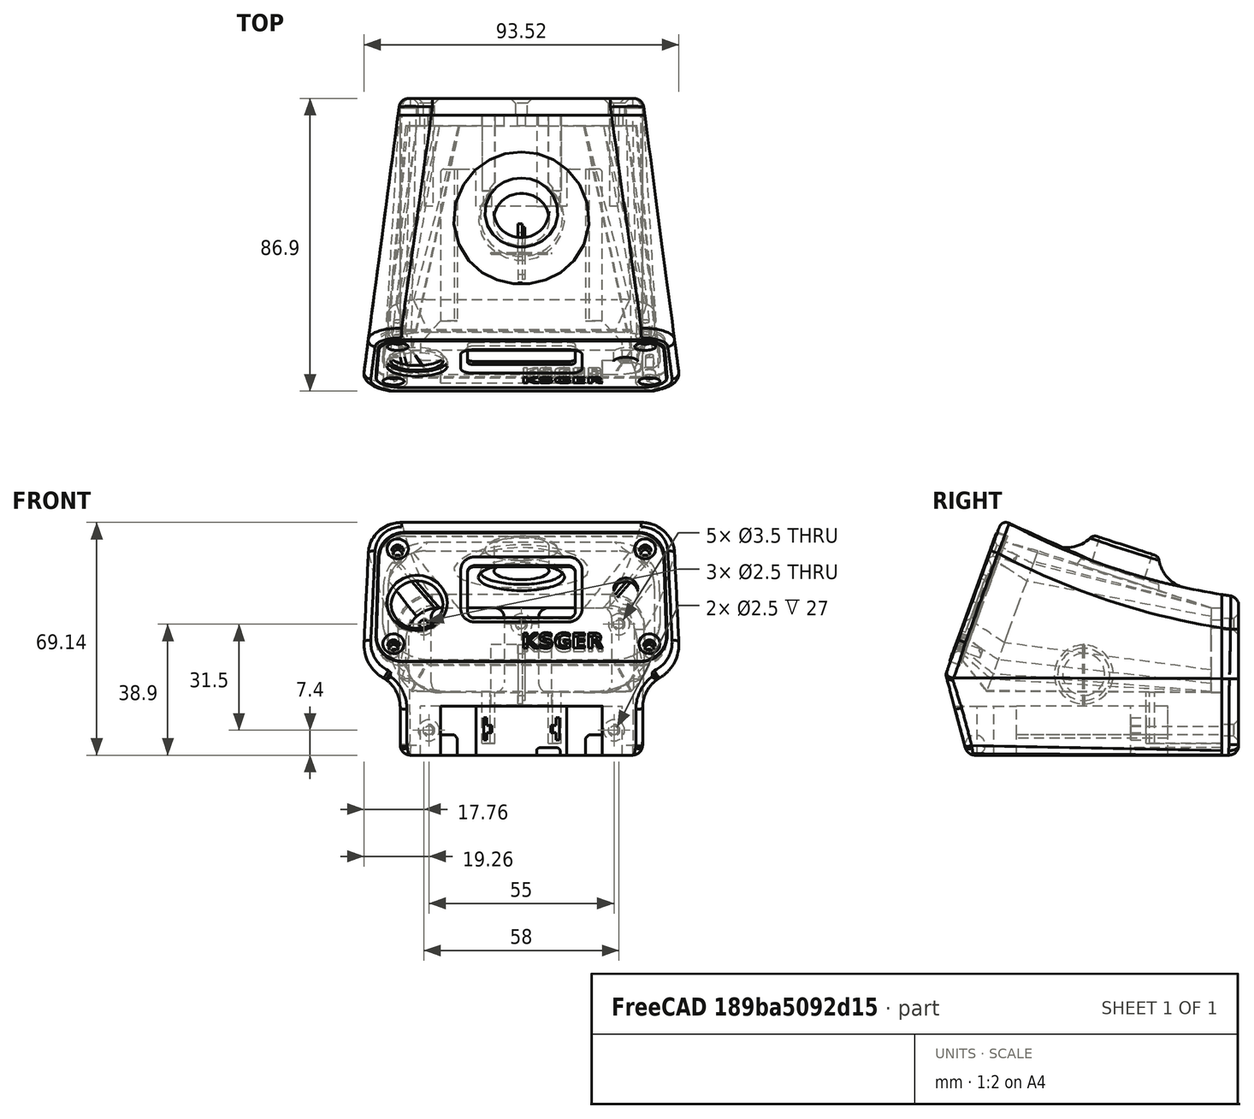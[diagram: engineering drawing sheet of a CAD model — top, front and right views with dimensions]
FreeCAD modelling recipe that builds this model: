
FCSTD DOCUMENT  (FreeCAD 2022.709R28846 (Git))
Label: solder_station5a_snap
License: All rights reserved
LicenseURL: http://en.wikipedia.org/wiki/All_rights_reserved
objects: Sketcher::SketchObject×22, PartDesign::Pocket×12, Part::FeaturePython×6, PartDesign::Fillet×6, Mesh::Feature×5, App::DocumentObjectGroup×4, PartDesign::Body×4, PartDesign::Chamfer×3, PartDesign::FeatureBase×2, PartDesign::Pad×2, PartDesign::Revolution×2, Spreadsheet::Sheet×1, Part::Plane×1, Part::Loft×1, Part::Extrusion×1, Part::MultiCommon×1, Part::Box×1, PartDesign::SubtractiveLoft×1, PartDesign::Groove×1, Part::Part2DObjectPython×1, +2 more types
note: 124 computed .brp shape members not serialized (recipe doc carries the construction recipe); baked Part::Feature solids carry a one-line shape summary decoded from their .brp

FEATURE [Sketcher::SketchObject] Sketch  label="RearSupport"
  ArcFitTolerance = 0
  AttachmentOffset = pos=(0,0,-37.8) rot=(0,0,1;0rad)
  AttachmentSupport = -> [XZ_Plane005]
  FullyConstrained = true
  MapMode = 5
  Placement = pos=(0,37.8,8.4e-15) rot=(1,0,0;1.5708rad)
  Support = -> [XZ_Plane005]
  TreeRank = 0
  expr: AttachmentOffset.Base.z = -<<param>>.mid_depth / 2 + <<param>>.wall
  expr: Constraints[24] = 3
  expr: Constraints[37] = <<param>>.bottom_height
  expr: Constraints[38] = <<param>>.floor
  expr: Constraints[39] = <<param>>.rear_height - <<param>>.wall
  expr: Constraints[47] = <<param>>.reart_screw_width2
  expr: Constraints[48] = <<param>>.rear_screw_width1
  expr: Constraints[49] = <<param>>.screw_hole
  expr: Constraints[50] = <<param>>.rear_screw_height
  expr: Constraints[51] = <<param>>.rear_screw_height
  expr: Constraints[52] = <<param>>.rear_screw_offset
  sketch-geometry (22):
    g0: LineSegment StartX=-23.8 StartY=19.8 StartZ=0 EndX=-8.1 EndY=19.8 EndZ=0
    g1: LineSegment StartX=26.8 StartY=16.8 StartZ=0 EndX=26.8 EndY=-2.4 EndZ=0
    g2: LineSegment StartX=23.8 StartY=-5.4 StartZ=0 EndX=8.1 EndY=-5.4 EndZ=0
    g3: LineSegment StartX=-26.8 StartY=-2.4 StartZ=0 EndX=-26.8 EndY=16.8 EndZ=0
    g4: LineSegment StartX=-5.1 StartY=16.8 StartZ=0 EndX=-5.1 EndY=-2.4 EndZ=0
    g5: LineSegment StartX=5.1 StartY=16.8 StartZ=0 EndX=5.1 EndY=-2.4 EndZ=0
    g6: LineSegment StartX=8.1 StartY=19.8 StartZ=0 EndX=23.8 EndY=19.8 EndZ=0
    g7: LineSegment StartX=-8.1 StartY=-5.4 StartZ=0 EndX=-23.8 EndY=-5.4 EndZ=0
    g8: ArcOfCircle CenterX=-8.1 CenterY=16.8 CenterZ=0 NormalX=0 NormalY=0 NormalZ=1 AngleXU=0 Radius=3 StartAngle=0 EndAngle=1.5708
    g9: ArcOfCircle CenterX=8.1 CenterY=16.8 CenterZ=0 NormalX=0 NormalY=0 NormalZ=1 AngleXU=0 Radius=3 StartAngle=1.5708 EndAngle=3.14159
    g10: ArcOfCircle CenterX=-8.1 CenterY=-2.4 CenterZ=0 NormalX=0 NormalY=0 NormalZ=1 AngleXU=0 Radius=3 StartAngle=4.71239 EndAngle=6.28319
    g11: ArcOfCircle CenterX=8.1 CenterY=-2.4 CenterZ=0 NormalX=0 NormalY=0 NormalZ=1 AngleXU=0 Radius=3 StartAngle=3.14159 EndAngle=4.71239
    g12: ArcOfCircle CenterX=-23.8 CenterY=16.8 CenterZ=0 NormalX=0 NormalY=0 NormalZ=1 AngleXU=0 Radius=3 StartAngle=1.5708 EndAngle=3.14159
    g13: ArcOfCircle CenterX=-23.8 CenterY=-2.4 CenterZ=0 NormalX=0 NormalY=0 NormalZ=1 AngleXU=0 Radius=3 StartAngle=3.14159 EndAngle=4.71239
    g14: ArcOfCircle CenterX=23.8 CenterY=16.8 CenterZ=0 NormalX=0 NormalY=0 NormalZ=1 AngleXU=0 Radius=3 StartAngle=3e-16 EndAngle=1.5708
    g15: ArcOfCircle CenterX=23.8 CenterY=-2.4 CenterZ=0 NormalX=0 NormalY=0 NormalZ=1 AngleXU=0 Radius=3 StartAngle=4.71239 EndAngle=6.28319
    g16: Circle [constr] CenterX=0 CenterY=-24 CenterZ=0 NormalX=0 NormalY=0 NormalZ=1 AngleXU=0 Radius=3
    g17: Circle CenterX=0 CenterY=14.9 CenterZ=0 NormalX=0 NormalY=0 NormalZ=1 AngleXU=0 Radius=1.25
    g18: Circle CenterX=-29 CenterY=14.9 CenterZ=0 NormalX=0 NormalY=0 NormalZ=1 AngleXU=0 Radius=1.25
    g19: Circle [constr] CenterX=-27.5 CenterY=-16.6 CenterZ=0 NormalX=0 NormalY=0 NormalZ=1 AngleXU=0 Radius=1.25
    g20: Circle [constr] CenterX=27.5 CenterY=-16.6 CenterZ=0 NormalX=0 NormalY=0 NormalZ=1 AngleXU=0 Radius=1.25
    g21: Circle CenterX=29 CenterY=14.9 CenterZ=0 NormalX=0 NormalY=0 NormalZ=1 AngleXU=0 Radius=1.25
  constraints (53):
    c: Horizontal(g0)
    c: Horizontal(g2)
    c: Vertical(g1)
    c: Vertical(g3)
    c: Vertical(g4)
    c: Vertical(g5)
    c: Tangent(g0,g6)
    c: Tangent(g2,g7)
    c: Tangent(g0,g8) = 1.5708
    c: Tangent(g4,g8) = 1.5708
    c: Tangent(g5,g9) = -1.5708
    c: Tangent(g6,g9) = 1.5708
    c: Tangent(g7,g10) = 1.5708
    c: Tangent(g4,g10) = 1.5708
    c: Tangent(g5,g11) = -1.5708
    c: Tangent(g2,g11) = 1.5708
    c: Tangent(g0,g12) = 1.5708
    c: Tangent(g3,g12) = 1.5708
    c: Tangent(g3,g13) = 1.5708
    c: Tangent(g7,g13) = 1.5708
    c: Tangent(g6,g14) = 1.5708
    c: Tangent(g1,g14) = 1.5708
    c: Tangent(g1,g15) = 1.5708
    c: Tangent(g2,g15) = 1.5708
    c: Radius(g9) = 3
    c: Equal(g12,g13)
    c: Equal(g13,g10)
    c: Equal(g10,g8)
    c: Equal(g11,g15)
    c: Equal(g15,g14)
    c: Equal(g14,g9)
    c: DistanceX(g4,g-1) = 5.1
    c: DistanceX(g5,g1) = 21.7
    c: Symmetric(g4,g5,g-2)
    c: Equal(g7,g2)
    c: PointOnObject(g16,g-2)
    c: Radius(g16) = 3
    c: DistanceY(g16,g-1) = 24
    c: DistanceY(g16,g2) = 18.6
    c: DistanceY(g16,g6) = 43.8
    c: PointOnObject(g17,g-2)
    c: Equal(g21,g18)
    c: Equal(g18,g19)
    c: Equal(g19,g20)
    c: Equal(g18,g17)
    c: Symmetric(g20,g19,g-2)
    c: Symmetric(g18,g21,g-2)
    c: DistanceX(g19,g20) = 55
    c: DistanceX(g18,g21) = 58
    c: Diameter(g19) = 2.5
    c: DistanceY(g20,g21) = 31.5
    c: DistanceY(g20,g17) = 31.5
    c: DistanceY(g16,g19) = 7.4
FEATURE [Spreadsheet::Sheet] Spreadsheet  label="param"
  PythonMode = false
  ShowCells = 0
  TreeRank = 0
  cells = A1=Body; B2=top_depth; C2(top_depth)=70; B3=mid_depth; C3(mid_depth)=82; D3=half is rear reference; B4=bottom_depth; C4(bottom_depth)=75; B6=bottom_width; C6(bottom_width)=72; B7=bottom_height; C7(bottom_height)=24; B8=bottom_angle; C8(bottom_angle)=15; B10=rear_width; C10(rear_width)=72; B11=rear_height; C11(rear_height)=47; F11=41; B13=mid_width; C13(mid_width)=80; B14=mid_height; C14(mid_height)=56; F14=50; B16=front_width1; C16(front_width1)=92; D16=@top; E16=upper; F16=91; B17=front_width2; C17(front_width2)=95; D17=@mid; E17=lower; F17=94; B18=front_height; C18(front_height)=70; F18=64; B19=front_angle; C19(front_angle)=20; B21=wall; C21(wall)=3.2; B22=radius_big; C22(radius_big)=10; B23=radius_small; C23(radius_small)=3; B24=arch; C24(arch)=200; A26=Button; B27=button_offset; C27(button_offset)=10; B28=button_inside_dia; C28(button_inside_dia)=20; B29=button_outside_dia; C29(button_outside_dia)=22; B30=button_height; C30(button_height)=30.6; F30=26; B31=button_extension; C31(button_extension)=8; B32=button_fillet; C32(button_fillet)=12; B33=button_angle; C33(button_angle)=-18; F33=-17; B34=button_hole; C34(button_hole)=16.4; B35=button_hole_center; C35(button_hole_center)=-0.5; A37=Battery Cuts; B38=batt_carveout; C38(batt_carveout)=14.6; B39=batt_rail; C39(batt_rail)=6; B40=batt_rail_length; C40(batt_rail_length)=45; A42=Terminals; B43=terminal_height; C43(terminal_height)=6.6; B44=terminal_thickness; C44(terminal_thickness)=1; B45=terminal_seperation; C45(terminal_seperation)=21.5; B46=terminal_offset; C46(terminal_offset)=4.5; B47=terminal_depth; C47(terminal_depth)=22.5; A49=Box Interior; B50=floor; C50(floor)=18.6; B51=rear_inside_width; C51(rear_inside_width)==C10 - C21; D51=calc; B52=rear_inside_height; C52(rear_inside_height)==C11 - C21; D52=calc; B53=mid_inside_width; C53(mid_inside_width)==C13; D53=calc; B54=mid_inside_height; C54(mid_inside_height)==C14 + 7; D54=calc; F54=6; B55=front_inside_width1; C55(front_inside_width1)==C62 - C58 * 2; D55=calc; E55=upper; B56=front_inside_width2; C56(front_inside_width2)==C63 - C58 * 2; D56=calc; E56=lower; B57=front_inside_height; C57(front_inside_height)==C64 - C59 * 2; D57=calc; B58=front_width_lip_width; C58(front_width_lip_width)=3; B59=front_inside_lip_height; C59(front_inside_lip_height)=2; A61=Face; B62=face_width1; C62(face_width1)==84 + 1; B63=face_width2; C63(face_width2)==85.5 + 1; B64=face_height; C64(face_height)=41; F64=35; B65=face_thickness; C65(face_thickness)=3; B66=face_radius; C66(face_radius)=8; B67=face_offset; C67(face_offset)=2.8; F67=2.8; A69=Screws; B70=screw_hole; C70(screw_hole)=2.5; B72=front_screw_width1; C72(front_screw_width1)=73.5; D72=upper; B73=front_screw_width2; C73(front_screw_width2)=76; D73=lower; B74=front_screw_height; C74(front_screw_height)=30; F74=24; B75=front_screw_offset; C75(front_screw_offset)=5.5; B77=rear_screw_width1; C77(rear_screw_width1)=58; B78=reart_screw_width2; C78(reart_screw_width2)=55; B79=rear_screw_height; C79(rear_screw_height)=31.5; F79=25.5; B80=rear_screw_offset; C80(rear_screw_offset)=7.4; A82=Back; B83=back_thickness; C83(back_thickness)=5
FEATURE [Sketcher::SketchObject] Sketch008  label="SketchButtonHole"
  ArcFitTolerance = 0
  AttachmentOffset = pos=(0,-0.5,30.6) rot=(1,0,0;-0.314159rad)
  AttachmentSupport = -> [XY_Plane005]
  FullyConstrained = true
  MapMode = 5
  Placement = pos=(0,-0.5,30.6) rot=(1,0,0;5.96903rad)
  Support = -> [XY_Plane005]
  TreeRank = 0
  expr: AttachmentOffset.Base.y = <<param>>.button_hole_center
  expr: AttachmentOffset.Base.z = <<param>>.button_height
  expr: AttachmentOffset.Rotation.Angle = <<param>>.button_angle
  expr: Constraints[0] = <<param>>.button_hole
  expr: Constraints[2] = <<param>>.button_offset
  sketch-geometry (1):
    g0: Circle CenterX=0 CenterY=10 CenterZ=0 NormalX=0 NormalY=0 NormalZ=1 AngleXU=0 Radius=8.2
  constraints (3):
    c: Diameter(g0) = 16.4
    c: PointOnObject(g0,g-2)
    c: DistanceY(g-1,g0) = 10
FEATURE [Sketcher::SketchObject] Sketch012  label="SketchSide"
  ArcFitTolerance = 0
  AttachmentOffset = pos=(2.5,0,0) rot=(0,0,1;0rad)
  AttachmentSupport = -> [YZ_Plane006]
  FullyConstrained = true
  MapMode = 5
  Placement = pos=(6e-16,2.5,-6e-16) rot=(0.57735,0.57735,0.57735;2.0944rad)
  Support = -> [YZ_Plane006]
  TreeRank = 0
  expr: AttachmentOffset.Base.x = <<param>>.back_thickness / 2
  expr: Constraints[14] = <<param>>.bottom_height
  expr: Constraints[15] = <<param>>.radius_small
  expr: Constraints[16] = 90 - <<param>>.bottom_angle
  expr: Constraints[17] = 90 - <<param>>.front_angle
  expr: Constraints[21] = <<param>>.front_height
  expr: Constraints[4] = <<param>>.rear_height - <<param>>.bottom_height
  expr: Constraints[5] = <<param>>.arch
  expr: Constraints[6] = <<param>>.mid_depth + <<param>>.back_thickness
  sketch-geometry (7):
    g0: LineSegment StartX=43.5 StartY=0 StartZ=0 EndX=43.5 EndY=23 EndZ=0
    g1: LineSegment StartX=-43.5 StartY=0 StartZ=0 EndX=-26.7574 EndY=46 EndZ=0
    g2: ArcOfCircle CenterX=69.5235 CenterY=221.3 CenterZ=0 NormalX=0 NormalY=0 NormalZ=1 AngleXU=0 Radius=200 StartAngle=4.21013 EndAngle=4.5819
    g3: LineSegment StartX=-43.5 StartY=0 StartZ=0 EndX=-37.665 EndY=-21.7765 EndZ=0
    g4: LineSegment StartX=-34.7673 StartY=-24 StartZ=0 EndX=43.5 EndY=-24 EndZ=0
    g5: LineSegment StartX=43.5 StartY=-24 StartZ=0 EndX=43.5 EndY=0 EndZ=0
    g6: ArcOfCircle CenterX=-34.7672 CenterY=-21 CenterZ=0 NormalX=0 NormalY=0 NormalZ=1 AngleXU=0 Radius=3 StartAngle=3.4034 EndAngle=4.71238
  constraints (22):
    c: PointOnObject(g1,g-1)
    c: Vertical(g0)
    c: Coincident(g2,g0)
    c: Symmetric(g1,g0,g-2)
    c: DistanceY(g0,g0) = 23
    c: Radius(g2) = 200
    c: DistanceX(g1,g0) = 87
    c: Horizontal(g4)
    c: Coincident(g5,g4)
    c: Vertical(g5)
    c: Coincident(g6,g3)
    c: Coincident(g6,g4)
    c: Tangent(g6,g4)
    c: Tangent(g6,g3)
    c: DistanceY(g4,g-1) = 24
    c: Radius(g6) = 3
    c: Angle(g3,g-1) = 1.309
    c: Angle(g-1,g1) = 1.22173
    c: Coincident(g3,g1)
    c: Coincident(g5,g0)
    c: Coincident(g2,g1)
    c: DistanceY(g4,g1) = 70
FEATURE [Sketcher::SketchObject] Sketch018  label="SketchBat1"
  ArcFitTolerance = 0
  AttachmentOffset = pos=(0,0,-24) rot=(0,0,1;0rad)
  AttachmentSupport = -> [XY_Plane005]
  FullyConstrained = true
  MapMode = 5
  Placement = pos=(0,0,-24) rot=(0,0,1;0rad)
  Support = -> [XY_Plane005]
  TreeRank = 0
  expr: AttachmentOffset.Base.z = -<<param>>.bottom_height
  expr: Constraints[63] = <<param>>.batt_rail_length
  expr: Constraints[64] = <<param>>.mid_depth / 2
  sketch-geometry (21):
    g0: LineSegment StartX=-24 StartY=-41.7082 StartZ=0 EndX=24 EndY=-41.7082 EndZ=0
    g1: LineSegment StartX=24 StartY=-41.7082 StartZ=0 EndX=24 EndY=-31.7082 EndZ=0
    g2: LineSegment StartX=24 StartY=-31.7082 StartZ=0 EndX=30 EndY=-31.7082 EndZ=0
    g3: LineSegment StartX=30 StartY=-31.7082 StartZ=0 EndX=30 EndY=-26.7082 EndZ=0
    g4: LineSegment StartX=30 StartY=-26.7082 StartZ=0 EndX=24 EndY=-20 EndZ=0
    g5: LineSegment StartX=24 StartY=-20 StartZ=0 EndX=24 EndY=24 EndZ=0
    g6: LineSegment StartX=13.5 StartY=24 StartZ=0 EndX=13.5 EndY=14 EndZ=0
    g7: LineSegment StartX=13.5 StartY=14 StartZ=0 EndX=-13.5 EndY=14 EndZ=0
    g8: LineSegment StartX=-13.5 StartY=14 StartZ=0 EndX=-13.5 EndY=24 EndZ=0
    g9: LineSegment StartX=-24 StartY=24 StartZ=0 EndX=-24 EndY=-20 EndZ=0
    g10: LineSegment StartX=-24 StartY=-20 StartZ=0 EndX=-30 EndY=-26.7082 EndZ=0
    g11: LineSegment StartX=-30 StartY=-26.7082 StartZ=0 EndX=-30 EndY=-31.7082 EndZ=0
    g12: LineSegment StartX=-30 StartY=-31.7082 StartZ=0 EndX=-24 EndY=-31.7082 EndZ=0
    g13: LineSegment StartX=-24 StartY=-31.7082 StartZ=0 EndX=-24 EndY=-41.7082 EndZ=0
    g14: Circle [constr] CenterX=0 CenterY=41 CenterZ=0 NormalX=0 NormalY=0 NormalZ=1 AngleXU=0 Radius=4
    g15: ArcOfCircle CenterX=-14.5 CenterY=24 CenterZ=0 NormalX=0 NormalY=0 NormalZ=1 AngleXU=0 Radius=1 StartAngle=6.28318 EndAngle=7.85399
    g16: LineSegment StartX=-23 StartY=25 StartZ=0 EndX=-14.5 EndY=25 EndZ=0
    g17: LineSegment StartX=14.5 StartY=25 StartZ=0 EndX=23 EndY=25 EndZ=0
    g18: ArcOfCircle CenterX=-23 CenterY=24 CenterZ=0 NormalX=0 NormalY=0 NormalZ=1 AngleXU=0 Radius=1 StartAngle=1.57079 EndAngle=3.1416
    g19: ArcOfCircle CenterX=14.5 CenterY=24 CenterZ=0 NormalX=0 NormalY=0 NormalZ=1 AngleXU=0 Radius=1 StartAngle=1.5708 EndAngle=3.14159
    g20: ArcOfCircle CenterX=23 CenterY=24 CenterZ=0 NormalX=0 NormalY=0 NormalZ=1 AngleXU=0 Radius=1.00001 StartAngle=2.75124e-06 EndAngle=1.5708
  constraints (65):
    c: Horizontal(g0)
    c: Coincident(g1,g0)
    c: Vertical(g1)
    c: Coincident(g2,g1)
    c: Horizontal(g2)
    c: Coincident(g3,g2)
    c: Coincident(g3,g4)
    c: Vertical(g5)
    c: Coincident(g6,g7)
    c: Coincident(g7,g8)
    c: Vertical(g8)
    c: Vertical(g9)
    c: Coincident(g10,g11)
    c: Vertical(g11)
    c: Coincident(g11,g12)
    c: Horizontal(g12)
    c: Coincident(g12,g13)
    c: Equal(g6,g8)
    c: Equal(g5,g9)
    c: Equal(g4,g10)
    c: Equal(g3,g11)
    c: Equal(g12,g2)
    c: Equal(g1,g13)
    c: Coincident(g13,g0)
    c: Vertical(g13)
    c: DistanceX(g7,g7) = 27
    c: Symmetric(g7,g6,g-2)
    c: Distance(g4) = 9
    c: Vertical(g3)
    c: DistanceY(g3,g3) = 5
    c: DistanceX(g2,g2) = 6
    c: DistanceY(g1,g1) = 10
    c: DistanceX(g0,g0) = 48
    c: PointOnObject(g14,g-2)
    c: Coincident(g9,g10)
    c: Coincident(g5,g4)
    c: Coincident(g15,g8)
    c: Coincident(g16,g15)
    c: Tangent(g15,g8)
    c: Horizontal(g16)
    c: Horizontal(g17)
    c: DistanceX(g9,g5) = 48
    c: Symmetric(g4,g9,g-2)
    c: Equal(g16,g17)
    c: Coincident(g18,g9)
    c: Coincident(g18,g16)
    c: Equal(g18,g15)
    c: Tangent(g18,g16)
    c: Tangent(g18,g9)
    c: DistanceY(g6,g17) = 11
    c: Vertical(g6)
    c: Coincident(g19,g6)
    c: Coincident(g19,g17)
    c: Coincident(g20,g17)
    c: Coincident(g20,g5)
    c: Tangent(g20,g17)
    c: Tangent(g20,g5)
    c: Tangent(g19,g6)
    c: Tangent(g19,g17)
    c: Equal(g15,g19)
    c: Radius(g19) = 1
    c: Radius(g14) = 4
    c: DistanceY(g15,g14) = 16
    c: DistanceY(g9,g16) = 45
    c: DistanceY(g-1,g14) = 41
FEATURE [Sketcher::SketchObject] Sketch019  label="SketchBat2"
  ArcFitTolerance = 0
  AttachmentOffset = pos=(0,0,-25) rot=(0,0,1;0rad)
  AttachmentSupport = -> [XZ_Plane005]
  FullyConstrained = true
  MapMode = 5
  Placement = pos=(0,25,5.6e-15) rot=(1,0,0;1.5708rad)
  Support = -> [XZ_Plane005]
  TreeRank = 0
  expr: AttachmentOffset.Base.z = -<<param>>.mid_depth / 2 + 16
  expr: Constraints[17] = <<param>>.bottom_height
  expr: Constraints[18] = <<param>>.batt_rail
  expr: Constraints[19] = 48.01mm
  sketch-geometry (10):
    g0: LineSegment StartX=-24.005 StartY=-18 StartZ=0 EndX=-20.005 EndY=-18 EndZ=0
    g1: LineSegment StartX=-19.005 StartY=-24 StartZ=0 EndX=-24.005 EndY=-24 EndZ=0
    g2: LineSegment StartX=-24.005 StartY=-24 StartZ=0 EndX=-24.005 EndY=-18 EndZ=0
    g3: LineSegment StartX=24.005 StartY=-18 StartZ=0 EndX=20.005 EndY=-18 EndZ=0
    g4: LineSegment StartX=19.005 StartY=-24 StartZ=0 EndX=24.005 EndY=-24 EndZ=0
    g5: LineSegment StartX=24.005 StartY=-24 StartZ=0 EndX=24.005 EndY=-18 EndZ=0
    g6: LineSegment StartX=-19.005 StartY=-19 StartZ=0 EndX=-19.005 EndY=-24 EndZ=0
    g7: LineSegment StartX=19.005 StartY=-24 StartZ=0 EndX=19.005 EndY=-19 EndZ=0
    g8: LineSegment StartX=-20.005 StartY=-18 StartZ=0 EndX=-19.005 EndY=-19 EndZ=0
    g9: LineSegment StartX=19.005 StartY=-19 StartZ=0 EndX=20.005 EndY=-18 EndZ=0
  constraints (29):
    c: Coincident(g1,g2)
    c: Coincident(g2,g0)
    c: Horizontal(g0)
    c: Horizontal(g1)
    c: Vertical(g2)
    c: Coincident(g4,g5)
    c: Coincident(g5,g3)
    c: Horizontal(g3)
    c: Horizontal(g4)
    c: Vertical(g5)
    c: Coincident(g6,g1)
    c: Vertical(g6)
    c: Equal(g1,g4)
    c: Coincident(g7,g4)
    c: Vertical(g7)
    c: Equal(g6,g7)
    c: Symmetric(g1,g4,g-2)
    c: DistanceY(g1,g-1) = 24
    c: DistanceY(g4,g3) = 6
    c: DistanceX(g1,g4) = 48.01
    c: DistanceX(g4,g4) = 5
    c: Coincident(g8,g0)
    c: Coincident(g8,g6)
    c: Coincident(g9,g7)
    c: Coincident(g9,g3)
    c: Equal(g0,g3)
    c: Equal(g2,g5)
    c: DistanceX(g0,g0) = 4
    c: DistanceY(g1,g6) = 5
FEATURE [Sketcher::SketchObject] Sketch021  label="SketchButton"
  ArcFitTolerance = 0
  AttachmentOffset = pos=(10,30.6,0) rot=(0,0,1;-0.314159rad)
  AttachmentSupport = -> [YZ_Plane005]
  FullyConstrained = true
  MapMode = 5
  Placement = pos=(-4.6e-15,10,30.6) rot=(-0.506732,-0.697457,-0.506732;4.35963rad)
  Support = -> [YZ_Plane005]
  TreeRank = 0
  expr: AttachmentOffset.Base.x = <<param>>.button_offset
  expr: AttachmentOffset.Base.y = <<param>>.button_height
  expr: AttachmentOffset.Rotation.Angle = <<param>>.button_angle
  expr: Constraints[6] = <<param>>.button_extension
  expr: Constraints[7] = <<param>>.button_outside_dia / 2
  sketch-geometry (5):
    g0: LineSegment StartX=0 StartY=0 StartZ=0 EndX=0 EndY=8 EndZ=0
    g1: LineSegment StartX=0 StartY=8 StartZ=0 EndX=9 EndY=8 EndZ=0
    g2: LineSegment StartX=0 StartY=0 StartZ=0 EndX=11 EndY=0 EndZ=0
    g3: LineSegment StartX=11 StartY=0 StartZ=0 EndX=11 EndY=6 EndZ=0
    g4: ArcOfCircle CenterX=9 CenterY=6 CenterZ=0 NormalX=0 NormalY=0 NormalZ=1 AngleXU=0 Radius=2 StartAngle=1e-16 EndAngle=1.5708
  constraints (13):
    c: Coincident(g0,g-1)
    c: PointOnObject(g0,g-2)
    c: Coincident(g1,g0)
    c: Horizontal(g1)
    c: Coincident(g2,g0)
    c: Horizontal(g2)
    c: DistanceY(g0,g0) = 8
    c: DistanceX(g2,g2) = 11
    c: Coincident(g3,g2)
    c: Vertical(g3)
    c: Radius(g4) = 2
    c: Tangent(g4,g1) = 1.5708
    c: Tangent(g4,g3) = -1.5708
FEATURE [Sketcher::SketchObject] Sketch022  label="SketchRearInside"
  ArcFitTolerance = 0
  AttachmentOffset = pos=(0,0,-37.8) rot=(0,0,1;0rad)
  AttachmentSupport = -> [XZ_Plane005]
  FullyConstrained = true
  MapMode = 5
  Placement = pos=(0,37.8,8.4e-15) rot=(1,0,0;1.5708rad)
  Support = -> [XZ_Plane005]
  TreeRank = 0
  expr: AttachmentOffset.Base.z = -<<param>>.mid_depth / 2 + <<param>>.wall
  expr: Constraints[12] = <<param>>.radius_big
  expr: Constraints[18] = <<param>>.rear_inside_width
  expr: Constraints[26] = <<param>>.bottom_height
  expr: Constraints[27] = <<param>>.rear_inside_height
  expr: Constraints[29] = <<param>>.floor
  sketch-geometry (9):
    g0: LineSegment StartX=-34.4 StartY=9.80003 StartZ=0 EndX=-34.4 EndY=4.59997 EndZ=0
    g1: LineSegment StartX=-24.4 StartY=-5.4 StartZ=0 EndX=24.4 EndY=-5.4 EndZ=0
    g2: LineSegment StartX=34.4 StartY=4.59997 StartZ=0 EndX=34.4 EndY=9.80003 EndZ=0
    g3: LineSegment StartX=-24.4 StartY=19.8 StartZ=0 EndX=24.4 EndY=19.8 EndZ=0
    g4: ArcOfCircle CenterX=24.4 CenterY=9.8 CenterZ=0 NormalX=0 NormalY=0 NormalZ=1 AngleXU=0 Radius=10 StartAngle=3.49027e-06 EndAngle=1.57079
    g5: ArcOfCircle CenterX=24.4 CenterY=4.6 CenterZ=0 NormalX=0 NormalY=0 NormalZ=1 AngleXU=0 Radius=10 StartAngle=4.71239 EndAngle=6.28318
    g6: ArcOfCircle CenterX=-24.4 CenterY=9.8 CenterZ=0 NormalX=0 NormalY=0 NormalZ=1 AngleXU=0 Radius=10 StartAngle=1.5708 EndAngle=3.14159
    g7: ArcOfCircle CenterX=-24.4 CenterY=4.6 CenterZ=0 NormalX=0 NormalY=0 NormalZ=1 AngleXU=0 Radius=10 StartAngle=3.1416 EndAngle=4.71239
    g8: Circle [constr] CenterX=0 CenterY=-24 CenterZ=0 NormalX=0 NormalY=0 NormalZ=1 AngleXU=0 Radius=3
  constraints (30):
    c: Vertical(g0)
    c: Horizontal(g1)
    c: Vertical(g2)
    c: Horizontal(g3)
    c: Equal(g3,g1)
    c: Equal(g0,g2)
    c: Coincident(g4,g3)
    c: Coincident(g4,g2)
    c: Coincident(g5,g2)
    c: Coincident(g5,g1)
    c: Coincident(g6,g0)
    c: Coincident(g6,g3)
    c: Radius(g6) = 10
    c: Equal(g6,g4)
    c: Equal(g4,g5)
    c: Coincident(g7,g1)
    c: Coincident(g7,g0)
    c: Equal(g5,g7)
    c: DistanceX(g0,g2) = 68.8
    c: Symmetric(g0,g2,g-2)
    c: Tangent(g4,g2)
    c: Tangent(g4,g3)
    c: Tangent(g5,g2)
    c: Tangent(g5,g1)
    c: Tangent(g6,g3)
    c: PointOnObject(g8,g-2)
    c: DistanceY(g8,g-1) = 24
    c: DistanceY(g8,g3) = 43.8
    c: Radius(g8) = 3
    c: DistanceY(g8,g1) = 18.6
FEATURE [Sketcher::SketchObject] Sketch024  label="SketchFaceCut"
  ArcFitTolerance = 0
  AttachmentOffset = pos=(0,0,37.6) rot=(1,0,0;-0.349066rad)
  AttachmentSupport = -> [XZ_Plane005]
  FullyConstrained = true
  MapMode = 5
  Placement = pos=(0,-37.6,-8.3e-15) rot=(-1,0,0;5.06145rad)
  Support = -> [XZ_Plane005]
  TreeRank = 0
  expr: AttachmentOffset.Base.z = <<param>>.mid_depth / 2 - <<param>>.face_thickness - 0.4
  expr: AttachmentOffset.Rotation.Angle = -<<param>>.front_angle
  expr: Constraints[13] = <<param>>.face_radius
  expr: Constraints[22] = <<param>>.face_width1
  expr: Constraints[23] = <<param>>.face_width2
  expr: Constraints[24] = <<param>>.face_offset
  expr: Constraints[25] = <<param>>.face_height
  sketch-geometry (8):
    g0: LineSegment StartX=-34.5035 StartY=43.8 StartZ=0 EndX=34.5037 EndY=43.8 EndZ=0
    g1: LineSegment StartX=42.5001 StartY=36.0399 StartZ=0 EndX=43.25 EndY=11.0399 EndZ=0
    g2: LineSegment StartX=35.2536 StartY=2.8 StartZ=0 EndX=-35.2536 EndY=2.8 EndZ=0
    g3: LineSegment StartX=-43.25 StartY=11.0399 StartZ=0 EndX=-42.4999 EndY=36.0399 EndZ=0
    g4: ArcOfCircle CenterX=34.5037 CenterY=35.8 CenterZ=0 NormalX=0 NormalY=0 NormalZ=1 AngleXU=0 Radius=8 StartAngle=0.0299879 EndAngle=1.5708
    g5: ArcOfCircle CenterX=35.2536 CenterY=10.8 CenterZ=0 NormalX=0 NormalY=0 NormalZ=1 AngleXU=0 Radius=8 StartAngle=4.71239 EndAngle=6.31317
    g6: ArcOfCircle CenterX=-34.5035 CenterY=35.8 CenterZ=0 NormalX=0 NormalY=0 NormalZ=1 AngleXU=0 Radius=8 StartAngle=1.5708 EndAngle=3.1116
    g7: ArcOfCircle CenterX=-35.2536 CenterY=10.8 CenterZ=0 NormalX=0 NormalY=0 NormalZ=1 AngleXU=0 Radius=8 StartAngle=3.1116 EndAngle=4.71239
  constraints (27):
    c: Horizontal(g0)
    c: Coincident(g4,g0)
    c: Coincident(g4,g1)
    c: Coincident(g5,g1)
    c: Coincident(g5,g2)
    c: Coincident(g6,g0)
    c: Coincident(g6,g3)
    c: Coincident(g7,g3)
    c: Coincident(g7,g2)
    c: Equal(g1,g3)
    c: Equal(g4,g6)
    c: Equal(g6,g7)
    c: Equal(g7,g5)
    c: Radius(g4) = 8
    c: Tangent(g6,g3)
    c: Tangent(g7,g3)
    c: Tangent(g7,g2)
    c: Tangent(g6,g0)
    c: Tangent(g4,g0)
    c: Tangent(g4,g1)
    c: Tangent(g5,g1)
    c: Tangent(g5,g2)
    c: DistanceX(g3,g1) = 85
    c: DistanceX(g3,g1) = 86.5
    c: DistanceY(g-1,g2) = 2.8
    c: DistanceY(g2,g0) = 41
    c: Symmetric(g2,g2,g-2)
FEATURE [Sketcher::SketchObject] Sketch025  label="SketchMidInside"
  ArcFitTolerance = 0
  AttachmentOffset = pos=(0,0,27) rot=(1,0,0;-0.349066rad)
  AttachmentSupport = -> [XZ_Plane005]
  FullyConstrained = true
  MapMode = 5
  Placement = pos=(0,-27,-6e-15) rot=(-1,0,0;5.06145rad)
  Support = -> [XZ_Plane005]
  TreeRank = 0
  expr: AttachmentOffset.Base.z = <<param>>.mid_depth / 2 - 14
  expr: AttachmentOffset.Rotation.Angle = -<<param>>.front_angle
  expr: Constraints[10] = <<param>>.radius_big + 1
  expr: Constraints[11] = <<param>>.floor
  expr: Constraints[12] = Spreadsheet.mid_inside_width - 1
  expr: Constraints[14] = <<param>>.mid_inside_height
  expr: Constraints[23] = <<param>>.mid_width - 15
  expr: Constraints[4] = <<param>>.bottom_height
  sketch-geometry (9):
    g0: LineSegment StartX=-28.5 StartY=39 StartZ=0 EndX=28.5 EndY=39 EndZ=0
    g1: LineSegment StartX=39.5 StartY=28 StartZ=0 EndX=39.5 EndY=10 EndZ=0
    g2: LineSegment StartX=32.5 StartY=-5.4 StartZ=0 EndX=-32.5 EndY=-5.4 EndZ=0
    g3: LineSegment StartX=-39.5 StartY=10 StartZ=0 EndX=-39.5 EndY=28 EndZ=0
    g4: Circle [constr] CenterX=0 CenterY=-24 CenterZ=0 NormalX=0 NormalY=0 NormalZ=1 AngleXU=0 Radius=3
    g5: ArcOfCircle CenterX=-28.5 CenterY=28 CenterZ=0 NormalX=0 NormalY=0 NormalZ=1 AngleXU=0 Radius=11 StartAngle=1.5708 EndAngle=3.14159
    g6: ArcOfCircle CenterX=28.5 CenterY=28 CenterZ=0 NormalX=0 NormalY=0 NormalZ=1 AngleXU=0 Radius=11 StartAngle=0 EndAngle=1.5708
    g7: ArcOfCircle CenterX=-15.553 CenterY=11.5941 CenterZ=0 NormalX=0 NormalY=0 NormalZ=1 AngleXU=0 Radius=24 StartAngle=3.20806 EndAngle=3.92838
    g8: ArcOfCircle CenterX=15.553 CenterY=11.5941 CenterZ=0 NormalX=0 NormalY=0 NormalZ=1 AngleXU=0 Radius=24 StartAngle=5.4964 EndAngle=6.21672
  constraints (25):
    c: Vertical(g1)
    c: Vertical(g3)
    c: PointOnObject(g4,g-2)
    c: Radius(g4) = 3
    c: DistanceY(g4,g-1) = 24
    c: Tangent(g3,g5) = 1.5708
    c: Tangent(g0,g5) = 1.5708
    c: Tangent(g0,g6) = 1.5708
    c: Tangent(g1,g6) = 1.5708
    c: Equal(g6,g5)
    c: Radius(g6) = 11
    c: DistanceY(g4,g2) = 18.6
    c: DistanceX(g3,g1) = 79
    c: Symmetric(g2,g2,g-2)
    c: DistanceY(g4,g0) = 63
    c: Symmetric(g0,g0,g-2)
    c: Equal(g3,g1)
    c: Coincident(g7,g2)
    c: Coincident(g8,g1)
    c: Coincident(g8,g2)
    c: Coincident(g7,g3)
    c: Equal(g8,g7)
    c: Radius(g8) = 24
    c: DistanceX(g2,g2) = 65
    c: DistanceY(g1,g1) = 18
FEATURE [Sketcher::SketchObject] Sketch026  label="SketchFrontScrews"
  ArcFitTolerance = 0
  AttachmentOffset = pos=(0,0,38) rot=(1,0,0;-0.349066rad)
  AttachmentSupport = -> [XZ_Plane005]
  FullyConstrained = true
  MapMode = 5
  Placement = pos=(0,-38,-8.4e-15) rot=(-1,0,0;5.06145rad)
  Support = -> [XZ_Plane005]
  TreeRank = 0
  expr: AttachmentOffset.Base.z = <<param>>.mid_depth / 2 - <<param>>.face_thickness
  expr: AttachmentOffset.Rotation.Angle = -<<param>>.front_angle
  expr: Constraints[0] = <<param>>.front_screw_width1
  expr: Constraints[13] = <<param>>.screw_hole
  expr: Constraints[1] = <<param>>.front_screw_width2
  expr: Constraints[2] = <<param>>.front_screw_height
  expr: Constraints[9] = <<param>>.face_offset + <<param>>.front_screw_offset
  sketch-geometry (6):
    g0: Circle CenterX=-36.75 CenterY=38.3 CenterZ=0 NormalX=0 NormalY=0 NormalZ=1 AngleXU=0 Radius=1.25
    g1: Circle CenterX=36.75 CenterY=38.3 CenterZ=0 NormalX=0 NormalY=0 NormalZ=1 AngleXU=0 Radius=1.25
    g2: Circle CenterX=-38 CenterY=8.3 CenterZ=0 NormalX=0 NormalY=0 NormalZ=1 AngleXU=0 Radius=1.25
    g3: Circle CenterX=38 CenterY=8.3 CenterZ=0 NormalX=0 NormalY=0 NormalZ=1 AngleXU=0 Radius=1.25
    g4: LineSegment [constr] StartX=-36.75 StartY=38.3 StartZ=0 EndX=36.75 EndY=38.3 EndZ=0
    g5: LineSegment [constr] StartX=-38 StartY=8.3 StartZ=0 EndX=38 EndY=8.3 EndZ=0
  constraints (14):
    c: DistanceX(g0,g1) = 73.5
    c: DistanceX(g2,g3) = 76
    c: DistanceY(g3,g1) = 30
    c: Coincident(g4,g0)
    c: Coincident(g4,g1)
    c: Coincident(g5,g2)
    c: Coincident(g5,g3)
    c: Symmetric(g2,g3,g-2)
    c: Symmetric(g0,g1,g-2)
    c: DistanceY(g-1,g3) = 8.3
    c: Equal(g0,g2)
    c: Equal(g2,g3)
    c: Equal(g3,g1)
    c: Diameter(g0) = 2.5
FEATURE [Sketcher::SketchObject] Sketch023  label="SketchFrontInside"
  ArcFitTolerance = 0
  AttachmentOffset = pos=(0,0,38) rot=(1,0,0;-0.349066rad)
  AttachmentSupport = -> [XZ_Plane005]
  ExternalGeometry = -> [Sketch026,Sketch024]
  FullyConstrained = true
  MapMode = 5
  Placement = pos=(0,-38,-8.4e-15) rot=(-1,0,0;5.06145rad)
  Support = -> [XZ_Plane005]
  TreeRank = 0
  expr: AttachmentOffset.Base.z = <<param>>.mid_depth / 2 - <<param>>.face_thickness
  expr: AttachmentOffset.Rotation.Angle = -<<param>>.front_angle
  sketch-geometry (16):
    g0: LineSegment StartX=-27.5 StartY=4.93681 StartZ=0 EndX=27.5 EndY=4.93681 EndZ=0
    g1: LineSegment StartX=27.5 StartY=41.9368 StartZ=0 EndX=-27.5 EndY=41.9368 EndZ=0
    g2: LineSegment StartX=-40.95 StartY=28.0001 StartZ=0 EndX=-41.25 EndY=18.0001 EndZ=0
    g3: LineSegment StartX=40.95 StartY=28 StartZ=0 EndX=41.25 EndY=18 EndZ=0
    g4: ArcOfCircle CenterX=36.75 CenterY=38.3 CenterZ=0 NormalX=0 NormalY=0 NormalZ=1 AngleXU=0 Radius=3 StartAngle=2.46996 EndAngle=5.23357
    g5: ArcOfCircle CenterX=27.5 CenterY=27.5965 CenterZ=0 NormalX=0 NormalY=0 NormalZ=1 AngleXU=0 Radius=13.4561 StartAngle=0.0299886 EndAngle=0.646116
    g6: ArcOfCircle CenterX=27.5 CenterY=27.5965 CenterZ=0 NormalX=0 NormalY=0 NormalZ=1 AngleXU=0 Radius=14.3403 StartAngle=1.06869 EndAngle=1.5708
    g7: ArcOfCircle CenterX=38 CenterY=8.3 CenterZ=0 NormalX=0 NormalY=0 NormalZ=1 AngleXU=0 Radius=3 StartAngle=1.04133 EndAngle=3.41706
    g8: ArcOfCircle CenterX=27.5 CenterY=17.5875 CenterZ=0 NormalX=0 NormalY=0 NormalZ=1 AngleXU=0 Radius=13.7562 StartAngle=5.77461 EndAngle=6.31317
    g9: ArcOfCircle CenterX=27.5 CenterY=17.5875 CenterZ=0 NormalX=0 NormalY=0 NormalZ=1 AngleXU=0 Radius=12.6507 StartAngle=4.71239 EndAngle=5.35813
    g10: ArcOfCircle CenterX=-36.75 CenterY=38.3 CenterZ=0 NormalX=0 NormalY=0 NormalZ=1 AngleXU=0 Radius=3 StartAngle=4.19123 EndAngle=6.95482
    g11: ArcOfCircle CenterX=-27.5 CenterY=27.5965 CenterZ=0 NormalX=0 NormalY=0 NormalZ=1 AngleXU=0 Radius=13.456 StartAngle=2.49548 EndAngle=3.1116
    g12: ArcOfCircle CenterX=-27.5 CenterY=27.5965 CenterZ=0 NormalX=0 NormalY=0 NormalZ=1 AngleXU=0 Radius=14.3403 StartAngle=1.5708 EndAngle=2.0729
    g13: ArcOfCircle CenterX=-38 CenterY=8.3 CenterZ=0 NormalX=0 NormalY=0 NormalZ=1 AngleXU=0 Radius=3 StartAngle=6.00771 EndAngle=8.38345
    g14: ArcOfCircle CenterX=-27.5 CenterY=17.5875 CenterZ=0 NormalX=0 NormalY=0 NormalZ=1 AngleXU=0 Radius=13.7562 StartAngle=3.1116 EndAngle=3.65016
    g15: ArcOfCircle CenterX=-27.5 CenterY=17.5875 CenterZ=0 NormalX=0 NormalY=0 NormalZ=1 AngleXU=0 Radius=12.6507 StartAngle=4.06665 EndAngle=4.71239
  constraints (42):
    c: Symmetric(g0,g0,g-2)
    c: Symmetric(g1,g1,g-2)
    c: DistanceY(g3,g3) = 10
    c: Equal(g3,g2)
    c: Equal(g1,g0)
    c: DistanceX(g1,g1) = 55
    c: Coincident(g4,g-3)
    c: Coincident(g5,g4)
    c: Coincident(g6,g4)
    c: Radius(g4) = 3
    c: Tangent(g5,g3) = 1.5708
    c: Parallel(g3,g-8)
    c: Tangent(g6,g1) = -1.5708
    c: DistanceX(g3,g-8) = 2
    c: Parallel(g-7,g2)
    c: DistanceX(g-7,g2) = 2
    c: Coincident(g7,g-4)
    c: Coincident(g8,g7)
    c: Coincident(g9,g7)
    c: Tangent(g8,g3) = 1.5708
    c: Tangent(g9,g0) = -1.5708
    c: Coincident(g9,g8)
    c: Coincident(g5,g6)
    c: DistanceY(g-10,g0) = 2
    c: DistanceY(g1,g-9) = 2
    c: Coincident(g10,g-6)
    c: Coincident(g11,g10)
    c: Coincident(g12,g10)
    c: Coincident(g13,g-5)
    c: Coincident(g14,g13)
    c: Coincident(g15,g13)
    c: Tangent(g12,g1) = -1.5708
    c: Tangent(g11,g2) = -1.5708
    c: Coincident(g11,g12)
    c: Coincident(g14,g15)
    c: Tangent(g14,g2) = -1.5708
    c: Tangent(g15,g0) = -1.5708
    c: Equal(g10,g13)
    c: Equal(g13,g7)
    c: Equal(g7,g4)
    c: Equal(g12,g6)
    c: DistanceY(g-1,g3) = 18
FEATURE [Sketcher::SketchObject] Sketch027  label="SketchButtonCarve"
  ArcFitTolerance = 0
  AttachmentOffset = pos=(10,28.6,0) rot=(0,0,1;-0.314159rad)
  AttachmentSupport = -> [YZ_Plane005]
  FullyConstrained = true
  MapMode = 5
  Placement = pos=(-4.1e-15,10,28.6) rot=(-0.506732,-0.697457,-0.506732;4.35963rad)
  Support = -> [YZ_Plane005]
  TreeRank = 0
  expr: AttachmentOffset.Base.x = <<param>>.button_offset
  expr: AttachmentOffset.Base.y = <<param>>.button_height - 2
  expr: AttachmentOffset.Rotation.Angle = <<param>>.button_angle
  expr: Constraints[12] = <<param>>.button_hole / 2 + 10
  expr: Constraints[6] = <<param>>.button_hole / 2 + 4
  sketch-geometry (4):
    g0: LineSegment StartX=0 StartY=2 StartZ=0 EndX=12.2 EndY=2 EndZ=0
    g1: ArcOfCircle CenterX=18.2 CenterY=3.09999 CenterZ=0 NormalX=0 NormalY=0 NormalZ=1 AngleXU=0 Radius=6.09999 StartAngle=3.32291 EndAngle=4.71239
    g2: LineSegment StartX=0 StartY=2 StartZ=0 EndX=0 EndY=-3 EndZ=0
    g3: LineSegment StartX=18.2 StartY=-3 StartZ=0 EndX=0 EndY=-3 EndZ=0
  constraints (13):
    c: Horizontal(g0)
    c: Coincident(g1,g0)
    c: Coincident(g2,g0)
    c: Coincident(g3,g1)
    c: Horizontal(g3)
    c: Tangent(g3,g1)
    c: DistanceX(g0,g0) = 12.2
    c: DistanceY(g2,g2) = 5
    c: Coincident(g2,g3)
    c: Vertical(g2)
    c: PointOnObject(g-1,g2)
    c: DistanceY(g2,g-1) = 3
    c: DistanceX(g3,g3) = 18.2
FEATURE [Sketcher::SketchObject] Sketch028  label="SketchTerminals"
  ArcFitTolerance = 0
  AttachmentSupport = -> [XZ_Plane005]
  FullyConstrained = true
  MapMode = 5
  Placement = pos=(0,0,0) rot=(1,0,0;1.5708rad)
  Support = -> [XZ_Plane005]
  TreeRank = 0
  expr: Constraints[17] = <<param>>.terminal_thickness
  expr: Constraints[18] = <<param>>.terminal_height
  expr: Constraints[21] = <<param>>.bottom_height
  expr: Constraints[22] = <<param>>.terminal_offset
  expr: Constraints[23] = <<param>>.terminal_seperation
  sketch-geometry (17):
    g0: LineSegment StartX=10.25 StartY=-12.9 StartZ=0 EndX=11.25 EndY=-12.9 EndZ=0
    g1: LineSegment StartX=11.25 StartY=-12.9 StartZ=0 EndX=11.25 EndY=-19.5 EndZ=0
    g2: LineSegment StartX=11.25 StartY=-19.5 StartZ=0 EndX=10.25 EndY=-19.5 EndZ=0
    g3: LineSegment StartX=10.25 StartY=-19.5 StartZ=0 EndX=10.25 EndY=-17.25 EndZ=0
    g4: LineSegment StartX=-10.25 StartY=-12.9 StartZ=0 EndX=-11.25 EndY=-12.9 EndZ=0
    g5: LineSegment StartX=-11.25 StartY=-12.9 StartZ=0 EndX=-11.25 EndY=-19.5 EndZ=0
    g6: LineSegment StartX=-11.25 StartY=-19.5 StartZ=0 EndX=-10.25 EndY=-19.5 EndZ=0
    g7: LineSegment StartX=-10.25 StartY=-19.5 StartZ=0 EndX=-10.25 EndY=-17.25 EndZ=0
    g8: Circle [constr] CenterX=0 CenterY=-24 CenterZ=0 NormalX=0 NormalY=0 NormalZ=1 AngleXU=0 Radius=3
    g9: LineSegment StartX=-10.25 StartY=-15.15 StartZ=0 EndX=-8.75 EndY=-15.15 EndZ=0
    g10: LineSegment StartX=-8.75 StartY=-15.15 StartZ=0 EndX=-8.75 EndY=-17.25 EndZ=0
    g11: LineSegment StartX=-8.75 StartY=-17.25 StartZ=0 EndX=-10.25 EndY=-17.25 EndZ=0
    g12: LineSegment StartX=-10.25 StartY=-15.15 StartZ=0 EndX=-10.25 EndY=-12.9 EndZ=0
    g13: LineSegment StartX=10.25 StartY=-15.15 StartZ=0 EndX=8.75 EndY=-15.15 EndZ=0
    g14: LineSegment StartX=8.75 StartY=-15.15 StartZ=0 EndX=8.75 EndY=-17.25 EndZ=0
    g15: LineSegment StartX=8.75 StartY=-17.25 StartZ=0 EndX=10.25 EndY=-17.25 EndZ=0
    g16: LineSegment StartX=10.25 StartY=-15.15 StartZ=0 EndX=10.25 EndY=-12.9 EndZ=0
  constraints (48):
    c: Coincident(g0,g1)
    c: Coincident(g1,g2)
    c: Coincident(g2,g3)
    c: Coincident(g16,g0)
    c: Horizontal(g0)
    c: Horizontal(g2)
    c: Vertical(g1)
    c: Vertical(g3)
    c: Coincident(g4,g5)
    c: Coincident(g5,g6)
    c: Coincident(g6,g7)
    c: Coincident(g12,g4)
    c: Horizontal(g4)
    c: Horizontal(g6)
    c: Vertical(g5)
    c: Vertical(g7)
    c: Equal(g4,g0)
    c: DistanceX(g4,g4) = 1
    c: DistanceY(g3,g16) = 6.6
    c: PointOnObject(g8,g-2)
    c: Radius(g8) = 3
    c: DistanceY(g8,g-1) = 24
    c: DistanceY(g8,g1) = 4.5
    c: DistanceX(g6,g1) = 21.5
    c: Symmetric(g4,g0,g-2)
    c: Horizontal(g9)
    c: Coincident(g10,g9)
    c: Vertical(g10)
    c: Coincident(g11,g10)
    c: Horizontal(g11)
    c: Coincident(g7,g11)
    c: Coincident(g12,g9)
    c: Tangent(g7,g12)
    c: Equal(g12,g7)
    c: Horizontal(g5,g1)
    c: DistanceY(g10,g10) = 2.1
    c: DistanceX(g9,g9) = 1.5
    c: Horizontal(g13)
    c: Coincident(g14,g13)
    c: Vertical(g14)
    c: Coincident(g15,g14)
    c: Horizontal(g15)
    c: Coincident(g3,g15)
    c: Coincident(g16,g13)
    c: Tangent(g3,g16)
    c: Equal(g16,g3)
    c: Equal(g13,g9)
    c: Equal(g14,g10)
FEATURE [Sketcher::SketchObject] Sketch029  label="SketchAccess"
  ArcFitTolerance = 0
  AttachmentOffset = pos=(0,0,-20.5) rot=(0,0,1;0rad)
  AttachmentSupport = -> [XY_Plane005]
  FullyConstrained = true
  MapMode = 5
  Placement = pos=(0,0,-20.5) rot=(0,0,1;0rad)
  Support = -> [XY_Plane005]
  TreeRank = 0
  expr: AttachmentOffset.Base.z = -<<param>>.bottom_height + <<param>>.terminal_offset - 1
  expr: Constraints[19] = <<param>>.mid_depth / 2
  expr: Constraints[22] = <<param>>.terminal_seperation + <<param>>.terminal_thickness * 2
  expr: Constraints[23] = <<param>>.terminal_depth
  sketch-geometry (12):
    g0: LineSegment StartX=-11.75 StartY=41 StartZ=0 EndX=-11.75 EndY=18.5 EndZ=0
    g1: LineSegment StartX=-11.75 StartY=18.5 StartZ=0 EndX=-9.25 EndY=18.5 EndZ=0
    g2: LineSegment StartX=-7.95 StartY=21 StartZ=0 EndX=-7.95 EndY=41 EndZ=0
    g3: LineSegment StartX=-7.95 StartY=41 StartZ=0 EndX=-11.75 EndY=41 EndZ=0
    g4: LineSegment StartX=7.95 StartY=41 StartZ=0 EndX=11.75 EndY=41 EndZ=0
    g5: LineSegment StartX=11.75 StartY=41 StartZ=0 EndX=11.75 EndY=18.5 EndZ=0
    g6: LineSegment StartX=11.75 StartY=18.5 StartZ=0 EndX=9.25 EndY=18.5 EndZ=0
    g7: LineSegment StartX=7.95 StartY=21 StartZ=0 EndX=7.95 EndY=41 EndZ=0
    g8: LineSegment StartX=9.25 StartY=18.5 StartZ=0 EndX=9.25 EndY=19.5 EndZ=0
    g9: LineSegment StartX=7.95 StartY=21 StartZ=0 EndX=9.25 EndY=19.5 EndZ=0
    g10: LineSegment StartX=-9.25 StartY=18.5 StartZ=0 EndX=-9.25 EndY=19.5 EndZ=0
    g11: LineSegment StartX=-9.25 StartY=19.5 StartZ=0 EndX=-7.95 EndY=21 EndZ=0
  constraints (35):
    c: Vertical(g0)
    c: Coincident(g0,g1)
    c: Vertical(g2)
    c: Coincident(g2,g3)
    c: Coincident(g3,g0)
    c: Horizontal(g3)
    c: Horizontal(g4)
    c: Coincident(g4,g5)
    c: Vertical(g5)
    c: Coincident(g5,g6)
    c: Horizontal(g6)
    c: Coincident(g7,g4)
    c: Vertical(g7)
    c: Equal(g3,g4)
    c: Equal(g0,g5)
    c: Horizontal(g1)
    c: Equal(g2,g7)
    c: Equal(g1,g6)
    c: Symmetric(g2,g4,g-2)
    c: DistanceY(g-1,g0) = 41
    c: DistanceX(g1,g1) = 2.5
    c: DistanceX(g0,g2) = 3.8
    c: DistanceX(g0,g5) = 23.5
    c: DistanceY(g5,g4) = 22.5
    c: DistanceY(g2,g2) = 20
    c: Coincident(g8,g6) = 23.5
    c: Vertical(g8) = 22
    c: Coincident(g9,g7)
    c: Coincident(g9,g8)
    c: Coincident(g10,g1)
    c: Coincident(g11,g10)
    c: Coincident(g11,g2)
    c: Equal(g8,g10)
    c: DistanceY(g8,g8) = 1
    c: Vertical(g10)
FEATURE [Sketcher::SketchObject] Sketch030  label="SketchFront"
  ArcFitTolerance = 0
  AttachmentOffset = pos=(0,0,41) rot=(0,0,1;0rad)
  AttachmentSupport = -> [XZ_Plane006]
  FullyConstrained = true
  MapMode = 5
  Placement = pos=(0,-41,-9.1e-15) rot=(1,0,0;1.5708rad)
  Support = -> [XZ_Plane006]
  TreeRank = 0
  expr: AttachmentOffset.Base.z = <<param>>.mid_depth / 2
  expr: Constraints[10] = <<param>>.front_width2
  expr: Constraints[11] = <<param>>.front_width2
  expr: Constraints[12] = <<param>>.front_height + 2
  expr: Constraints[22] = <<param>>.radius_big * 1.2
  expr: Constraints[27] = <<param>>.radius_big
  expr: Constraints[6] = <<param>>.radius_small
  expr: Constraints[7] = <<param>>.bottom_width
  expr: Constraints[9] = <<param>>.bottom_height
  sketch-geometry (12):
    g0: LineSegment StartX=-47.5 StartY=48 StartZ=0 EndX=47.5 EndY=48 EndZ=0
    g1: LineSegment StartX=47.5 StartY=48 StartZ=0 EndX=47.5 EndY=9.54506 EndZ=0
    g2: LineSegment StartX=36 StartY=-9.78755 StartZ=0 EndX=36 EndY=-21 EndZ=0
    g3: LineSegment StartX=33 StartY=-24 StartZ=0 EndX=-33 EndY=-24 EndZ=0
    g4: LineSegment StartX=-36 StartY=-21 StartZ=0 EndX=-36 EndY=-9.78755 EndZ=0
    g5: LineSegment StartX=-47.5 StartY=9.54506 StartZ=0 EndX=-47.5 EndY=48 EndZ=0
    g6: ArcOfCircle CenterX=-33 CenterY=-21 CenterZ=0 NormalX=0 NormalY=0 NormalZ=1 AngleXU=0 Radius=3 StartAngle=3.14159 EndAngle=4.71239
    g7: ArcOfCircle CenterX=33 CenterY=-21 CenterZ=0 NormalX=0 NormalY=0 NormalZ=1 AngleXU=0 Radius=3 StartAngle=4.71239 EndAngle=6.28319
    g8: ArcOfCircle CenterX=46 CenterY=-9.78755 CenterZ=0 NormalX=0 NormalY=0 NormalZ=1 AngleXU=0 Radius=10 StartAngle=2.06834 EndAngle=3.14159
    g9: ArcOfCircle CenterX=35.5 CenterY=9.54506 CenterZ=0 NormalX=0 NormalY=0 NormalZ=1 AngleXU=0 Radius=12 StartAngle=5.20994 EndAngle=6.28319
    g10: ArcOfCircle CenterX=-46 CenterY=-9.78755 CenterZ=0 NormalX=0 NormalY=0 NormalZ=1 AngleXU=0 Radius=10 StartAngle=0 EndAngle=1.07325
    g11: ArcOfCircle CenterX=-35.5 CenterY=9.54506 CenterZ=0 NormalX=0 NormalY=0 NormalZ=1 AngleXU=0 Radius=12 StartAngle=3.14159 EndAngle=4.21484
  constraints (30):
    c: Vertical(g2)
    c: Vertical(g4)
    c: Tangent(g4,g6) = 1.5708
    c: Tangent(g3,g6) = 1.5708
    c: Tangent(g3,g7) = 1.5708
    c: Tangent(g2,g7) = 1.5708
    c: Radius(g7) = 3
    c: DistanceX(g4,g2) = 72
    c: Symmetric(g3,g3,g-2)
    c: DistanceY(g3,g-1) = 24
    c: DistanceX(g5,g1) = 95
    c: DistanceX(g5,g1) = 95
    c: DistanceY(g3,g0) = 72
    c: Equal(g7,g6)
    c: Equal(g10,g8)
    c: Symmetric(g5,g1,g-2)
    c: Equal(g4,g2)
    c: Coincident(g8,g2)
    c: Coincident(g0,g1)
    c: Coincident(g5,g0)
    c: Symmetric(g0,g0,g-2)
    c: Equal(g9,g11)
    c: Radius(g9) = 12
    c: Tangent(g11,g5) = 1.5708
    c: Tangent(g1,g9) = 1.5708
    c: Tangent(g11,g10) = 1.5708
    c: Tangent(g8,g9) = 1.5708
    c: Radius(g8) = 10
    c: DistanceY(g8,g-1) = 1
    c: Tangent(g10,g4) = -1.5708
FEATURE [Sketcher::SketchObject] Sketch031  label="SketchRear"
  ArcFitTolerance = 0
  AttachmentOffset = pos=(0,0,-46) rot=(0,0,1;0rad)
  AttachmentSupport = -> [XZ_Plane006]
  FullyConstrained = true
  MapMode = 5
  Placement = pos=(0,46,1.02e-14) rot=(1,0,0;1.5708rad)
  Support = -> [XZ_Plane006]
  TreeRank = 0
  expr: AttachmentOffset.Base.z = -<<param>>.mid_depth / 2 - <<param>>.back_thickness
  expr: Constraints[15] = <<param>>.front_height + 2
  expr: Constraints[1] = <<param>>.radius_small
  expr: Constraints[2] = <<param>>.bottom_height
  expr: Constraints[3] = <<param>>.rear_width
  sketch-geometry (6):
    g0: LineSegment StartX=-33 StartY=-24 StartZ=0 EndX=33 EndY=-24 EndZ=0
    g1: LineSegment StartX=36 StartY=48 StartZ=0 EndX=-36 EndY=48 EndZ=0
    g2: ArcOfCircle CenterX=-33 CenterY=-21 CenterZ=0 NormalX=0 NormalY=0 NormalZ=1 AngleXU=0 Radius=3 StartAngle=3.14159 EndAngle=4.71239
    g3: ArcOfCircle CenterX=33 CenterY=-21 CenterZ=0 NormalX=0 NormalY=0 NormalZ=1 AngleXU=0 Radius=3 StartAngle=4.71239 EndAngle=6.28319
    g4: LineSegment StartX=36 StartY=-21 StartZ=0 EndX=36 EndY=48 EndZ=0
    g5: LineSegment StartX=-36 StartY=-21 StartZ=0 EndX=-36 EndY=48 EndZ=0
  constraints (19):
    c: Horizontal(g0)
    c: Radius(g3) = 3
    c: DistanceY(g0,g-1) = 24
    c: DistanceX(g2,g3) = 72
    c: Coincident(g4,g3)
    c: Vertical(g4)
    c: Coincident(g5,g2)
    c: Equal(g5,g4)
    c: Horizontal(g3,g3)
    c: Horizontal(g2,g2)
    c: Equal(g2,g3)
    c: Coincident(g0,g2)
    c: Coincident(g0,g3)
    c: Vertical(g2,g0)
    c: Vertical(g5)
    c: DistanceY(g0,g1) = 72
    c: Symmetric(g4,g5,g-2)
    c: Coincident(g4,g1)
    c: Coincident(g5,g1)
FEATURE [Part::Plane] Plane002  label="PlaneDivider"
  AttacherType = Attacher::AttachEngine3D
  AttachmentSupport = -> [XZ_Plane006]
  Length = 152
  Placement = pos=(-75,41,-75) rot=(1,0,0;1.5708rad)
  Support = -> [XZ_Plane006]
  TreeRank = 0
  Width = 150
  expr: Placement.Base.y = <<param>>.mid_depth / 2
FEATURE [Sketcher::SketchObject] Sketch032  label="SketchBack"
  ArcFitTolerance = 0
  AttachmentSupport = -> [XZ_Plane]
  FullyConstrained = true
  MapMode = 5
  Placement = pos=(0,0,0) rot=(1,0,0;1.5708rad)
  Support = -> [XZ_Plane]
  TreeRank = 0
  expr: Constraints[10] = <<param>>.rear_screw_width1
  expr: Constraints[11] = <<param>>.reart_screw_width2
  expr: Constraints[12] = <<param>>.rear_screw_height
  expr: Constraints[15] = <<param>>.rear_screw_offset
  expr: Constraints[1] = <<param>>.bottom_height
  expr: Constraints[2] = <<param>>.rear_width
  expr: Constraints[9] = <<param>>.screw_hole + 1
  sketch-geometry (6):
    g0: LineSegment [constr] StartX=36 StartY=-24 StartZ=0 EndX=-36 EndY=-24 EndZ=0
    g1: Circle CenterX=-29 CenterY=14.9 CenterZ=0 NormalX=0 NormalY=0 NormalZ=1 AngleXU=0 Radius=1.75
    g2: Circle CenterX=0 CenterY=14.9 CenterZ=0 NormalX=0 NormalY=0 NormalZ=1 AngleXU=0 Radius=1.75
    g3: Circle CenterX=29 CenterY=14.9 CenterZ=0 NormalX=0 NormalY=0 NormalZ=1 AngleXU=0 Radius=1.75
    g4: Circle CenterX=-27.5 CenterY=-16.6 CenterZ=0 NormalX=0 NormalY=0 NormalZ=1 AngleXU=0 Radius=1.75
    g5: Circle CenterX=27.5 CenterY=-16.6 CenterZ=0 NormalX=0 NormalY=0 NormalZ=1 AngleXU=0 Radius=1.75
  constraints (16):
    c: Symmetric(g0,g0,g-2)
    c: DistanceY(g0,g-1) = 24
    c: DistanceX(g0,g0) = 72
    c: Symmetric(g1,g3,g-2)
    c: Symmetric(g4,g5,g-2)
    c: Equal(g4,g1)
    c: Equal(g1,g2)
    c: Equal(g2,g3)
    c: Equal(g3,g5)
    c: Diameter(g1) = 3.5
    c: DistanceX(g1,g3) = 58
    c: DistanceX(g4,g5) = 55
    c: DistanceY(g5,g3) = 31.5
    c: Horizontal(g1,g2)
    c: PointOnObject(g2,g-2)
    c: DistanceY(g0,g5) = 7.4
FEATURE [Part::Loft] Loft
  Closed = false
  MaxDegree = 5
  Ruled = false
  Sections = -> [Sketch030,Sketch031]
  Solid = true
  TreeRank = 0
FEATURE [Part::Extrusion] Extrude
  Base = -> Sketch012
  Dir = (1,-1e-16,1e-16)
  DirMode = 2
  FaceMakerClass = Part::FaceMakerBullseye
  InnerTaperAngle = 0
  InnerTaperAngleRev = 0
  LengthFwd = 100
  LengthRev = 0
  Solid = true
  Symmetric = true
  TreeRank = 0
FEATURE [Part::MultiCommon] Common
  Shapes = -> [Extrude,Loft]
  TreeRank = 0
FEATURE [Part::FeaturePython] Slice  # WARN: FeaturePython — macro-defined, semantics opaque (R4)
  Base = -> Common
  Mode = 1
  Tolerance = 0
  Tools = -> [Plane002]
  TreeRank = 0
FEATURE [Part::FeaturePython] Slice_child0  label="Slice.Case"  # WARN: FeaturePython — macro-defined, semantics opaque (R4)
  Base = -> Slice
  FilterType = 1
  Invert = false
  OverrideMaxVal = 0
  TreeRank = 0
  WindowFrom = 80
  WindowTo = 100
  items = 0
FEATURE [Part::FeaturePython] Slice_child1  label="Slice.Back"  # WARN: FeaturePython — macro-defined, semantics opaque (R4)
  Base = -> Slice
  FilterType = 1
  Invert = false
  OverrideMaxVal = 0
  TreeRank = 0
  WindowFrom = 80
  WindowTo = 100
  items = 1
FEATURE [App::DocumentObjectGroup] GrExplode_Slice  label="Exploded Slice"
  ClaimAllChildren = true
  ExportMode = 1
  Group = -> [Slice_child0,Slice_child1]
  TreeRank = 0
  _GroupVersion = 1
FEATURE [App::DocumentObjectGroup] Group001  label="BaseShape"
  ClaimAllChildren = true
  ExportMode = 1
  Group = -> [Common,Sketch012,Sketch031,Sketch030,Plane002,GrExplode_Slice]
  TreeRank = 0
  _GroupVersion = 1
FEATURE [PartDesign::FeatureBase] BaseFeature  label="Back.BaseFeature"
  BaseFeature = -> Slice_child1
  NewSolid = false
  Suppress = false
  TreeRank = 0
FEATURE [PartDesign::Pocket] Pocket  label="Back.Pocket.Screws"
  BaseFeature = -> BaseFeature
  ClaimChildren = false
  Fit = 0
  FitJoin = 0
  InnerFit = 0
  InnerFitJoin = 0
  InnerTaperAngle = 0
  InnerTaperAngleRev = 0
  Length = 5
  Length2 = 100
  Midplane = true
  NewSolid = false
  Profile = -> Sketch032
  Suppress = false
  TreeRank = 0
  Type = 1
  _ProfileBasedVersion = 0
FEATURE [PartDesign::FeatureBase] BaseFeature001  label="Case.BaseFeature"
  BaseFeature = -> Slice_child0
  NewSolid = false
  Suppress = false
  TreeRank = 0
FEATURE [PartDesign::Pocket] Pocket001  label="Case.Pocket.Batt"
  BaseFeature = -> BaseFeature001
  ClaimChildren = false
  Fit = 0
  FitJoin = 0
  InnerFit = 0
  InnerFitJoin = 0
  InnerTaperAngle = 0
  InnerTaperAngleRev = 0
  Length = 14.6
  Length2 = 100
  NewSolid = false
  Profile = -> Sketch018
  Reversed = true
  Suppress = false
  TreeRank = 0
  Type = 0
  _ProfileBasedVersion = 0
  expr: Length = <<param>>.batt_carveout
FEATURE [PartDesign::Pad] Pad  label="Case.Pad.Batt"
  BaseFeature = -> Pocket001
  ClaimChildren = false
  Direction = (1,1,1)
  Fit = 0
  FitJoin = 0
  InnerFit = 0
  InnerFitJoin = 0
  InnerTaperAngle = 0
  InnerTaperAngleRev = 0
  Length = 45
  Length2 = 100
  NewSolid = false
  Profile = -> Sketch019
  Suppress = false
  TreeRank = 0
  Type = 0
  _ProfileBasedVersion = 0
  expr: Length = <<param>>.batt_rail_length
FEATURE [PartDesign::Pocket] Pocket002  label="Case.Pocket.Support"
  BaseFeature = -> Pad
  ClaimChildren = false
  Fit = 0
  FitJoin = 0
  InnerFit = 0
  InnerFitJoin = 0
  InnerTaperAngle = 0
  InnerTaperAngleRev = 0
  Length = 5
  Length2 = 100
  NewSolid = false
  Profile = -> Sketch
  Suppress = false
  TreeRank = 0
  Type = 0
  _ProfileBasedVersion = 0
FEATURE [PartDesign::Pocket] Pocket006  label="Case.Pocket.Terminal"
  BaseFeature = -> Pocket002
  ClaimChildren = false
  Fit = 0
  FitJoin = 0
  InnerFit = 0
  InnerFitJoin = 0
  InnerTaperAngle = 0
  InnerTaperAngleRev = 0
  Length = 18.5
  Length2 = 100
  NewSolid = false
  Profile = -> Sketch028
  Suppress = false
  TreeRank = 0
  Type = 0
  _ProfileBasedVersion = 0
  expr: Length = <<param>>.mid_depth / 2 - <<param>>.terminal_depth
FEATURE [PartDesign::Pocket] Pocket005  label="Case.Pocket.Access"
  BaseFeature = -> Pocket006
  ClaimChildren = false
  Fit = 0
  FitJoin = 0
  InnerFit = 0
  InnerFitJoin = 0
  InnerTaperAngle = 0
  InnerTaperAngleRev = 0
  Length = 22.5
  Length2 = 100
  NewSolid = false
  Profile = -> Sketch029
  Reversed = true
  Suppress = false
  TreeRank = 0
  Type = 0
  _ProfileBasedVersion = 0
  expr: Length = <<param>>.terminal_depth
FEATURE [Sketcher::SketchObject] Sketch033  label="SketchFace"
  ArcFitTolerance = 0
  AttachmentSupport = -> [XZ_Plane007]
  FullyConstrained = true
  MapMode = 5
  Placement = pos=(0,0,0) rot=(1,0,0;1.5708rad)
  Support = -> [XZ_Plane007]
  TreeRank = 0
  expr: Constraints[12] = <<param>>.face_radius
  expr: Constraints[21] = <<param>>.face_width1 - 0.4
  expr: Constraints[22] = <<param>>.face_width2 - 0.4
  expr: Constraints[23] = <<param>>.face_height - 0.4
  expr: Constraints[27] = <<param>>.screw_hole + 1
  expr: Constraints[28] = <<param>>.front_screw_width2 / 2
  expr: Constraints[29] = <<param>>.front_screw_width2 / 2
  expr: Constraints[30] = <<param>>.front_screw_width1 / 2
  expr: Constraints[31] = <<param>>.front_screw_width1 / 2
  expr: Constraints[32] = <<param>>.front_screw_height
  expr: Constraints[35] = <<param>>.front_screw_offset + <<param>>.face_offset
  expr: Constraints[48] = <<param>>.face_offset
  sketch-geometry (23):
    g0: LineSegment StartX=-34.3037 StartY=43.4 StartZ=0 EndX=34.3037 EndY=43.4 EndZ=0
    g1: LineSegment StartX=42.3 StartY=35.6438 StartZ=0 EndX=43.05 EndY=11.0438 EndZ=0
    g2: LineSegment StartX=35.0537 StartY=2.8 StartZ=0 EndX=-35.0537 EndY=2.8 EndZ=0
    g3: LineSegment StartX=-43.05 StartY=11.0438 StartZ=0 EndX=-42.3 EndY=35.6438 EndZ=0
    g4: ArcOfCircle CenterX=34.3037 CenterY=35.4 CenterZ=0 NormalX=0 NormalY=0 NormalZ=1 AngleXU=0 Radius=8 StartAngle=0.0304753 EndAngle=1.5708
    g5: ArcOfCircle CenterX=35.0537 CenterY=10.8 CenterZ=0 NormalX=0 NormalY=0 NormalZ=1 AngleXU=0 Radius=8 StartAngle=4.71239 EndAngle=6.31366
    g6: ArcOfCircle CenterX=-34.3037 CenterY=35.4 CenterZ=0 NormalX=0 NormalY=0 NormalZ=1 AngleXU=0 Radius=8 StartAngle=1.5708 EndAngle=3.11112
    g7: ArcOfCircle CenterX=-35.0537 CenterY=10.8 CenterZ=0 NormalX=0 NormalY=0 NormalZ=1 AngleXU=0 Radius=8 StartAngle=3.11111 EndAngle=4.71239
    g8: Circle CenterX=-36.75 CenterY=38.3 CenterZ=0 NormalX=0 NormalY=0 NormalZ=1 AngleXU=0 Radius=1.75
    g9: Circle CenterX=36.75 CenterY=38.3 CenterZ=0 NormalX=0 NormalY=0 NormalZ=1 AngleXU=0 Radius=1.75
    g10: Circle CenterX=-38 CenterY=8.3 CenterZ=0 NormalX=0 NormalY=0 NormalZ=1 AngleXU=0 Radius=1.75
    g11: Circle CenterX=38 CenterY=8.3 CenterZ=0 NormalX=0 NormalY=0 NormalZ=1 AngleXU=0 Radius=1.75
    g12: LineSegment StartX=-14 StartY=33.75 StartZ=0 EndX=14 EndY=33.75 EndZ=0
    g13: LineSegment StartX=16 StartY=31.75 StartZ=0 EndX=16 EndY=19.25 EndZ=0
    g14: LineSegment StartX=14 StartY=17.25 StartZ=0 EndX=-14 EndY=17.25 EndZ=0
    g15: LineSegment StartX=-16 StartY=19.25 StartZ=0 EndX=-16 EndY=31.75 EndZ=0
    g16: ArcOfCircle CenterX=-14 CenterY=31.75 CenterZ=0 NormalX=0 NormalY=0 NormalZ=1 AngleXU=0 Radius=2 StartAngle=1.5708 EndAngle=3.14159
    g17: ArcOfCircle CenterX=-14 CenterY=19.25 CenterZ=0 NormalX=0 NormalY=0 NormalZ=1 AngleXU=0 Radius=2 StartAngle=3.14159 EndAngle=4.71239
    g18: ArcOfCircle CenterX=14 CenterY=19.25 CenterZ=0 NormalX=0 NormalY=0 NormalZ=1 AngleXU=0 Radius=2 StartAngle=4.71239 EndAngle=6.28319
    g19: ArcOfCircle CenterX=14 CenterY=31.75 CenterZ=0 NormalX=0 NormalY=0 NormalZ=1 AngleXU=0 Radius=2 StartAngle=7e-16 EndAngle=1.5708
    g20: Circle CenterX=-31 CenterY=21.5 CenterZ=0 NormalX=0 NormalY=0 NormalZ=1 AngleXU=0 Radius=7.75
    g21: Circle CenterX=31 CenterY=25.5 CenterZ=0 NormalX=0 NormalY=0 NormalZ=1 AngleXU=0 Radius=3.6
    g22: LineSegment [constr] StartX=-69 StartY=25.5 StartZ=0 EndX=31 EndY=25.5 EndZ=0
  constraints (67):
    c: Coincident(g4,g0)
    c: Coincident(g4,g1)
    c: Coincident(g5,g1)
    c: Coincident(g5,g2)
    c: Coincident(g6,g0)
    c: Coincident(g6,g3)
    c: Coincident(g7,g3)
    c: Coincident(g7,g2)
    c: Equal(g1,g3)
    c: Equal(g4,g6)
    c: Equal(g6,g7)
    c: Equal(g7,g5)
    c: Radius(g4) = 8
    c: Tangent(g6,g3)
    c: Tangent(g7,g3)
    c: Tangent(g7,g2)
    c: Tangent(g6,g0)
    c: Tangent(g4,g0)
    c: Tangent(g4,g1)
    c: Tangent(g5,g1)
    c: Tangent(g5,g2)
    c: DistanceX(g3,g1) = 84.6
    c: DistanceX(g3,g1) = 86.1
    c: DistanceY(g2,g0) = 40.6
    c: Equal(g9,g8)
    c: Equal(g8,g10)
    c: Equal(g10,g11)
    c: Diameter(g8) = 3.5
    c: DistanceX(g10,g-1) = 38
    c: DistanceX(g-1,g11) = 38
    c: DistanceX(g-1,g9) = 36.75
    c: DistanceX(g8,g-1) = 36.75
    c: DistanceY(g11,g9) = 30
    c: Horizontal(g8,g9)
    c: Horizontal(g10,g11)
    c: DistanceY(g-1,g11) = 8.3
    c: Horizontal(g12)
    c: Horizontal(g14)
    c: Vertical(g13)
    c: Vertical(g15)
    c: Tangent(g15,g16) = 1.5708
    c: Tangent(g12,g16) = 1.5708
    c: Tangent(g15,g17) = 1.5708
    c: Tangent(g14,g17) = 1.5708
    c: Tangent(g14,g18) = 1.5708
    c: Tangent(g13,g18) = 1.5708
    c: Tangent(g12,g19) = 1.5708
    c: Tangent(g13,g19) = 1.5708
    c: DistanceY(g-1,g2) = 2.8
    c: Horizontal(g0)
    c: Symmetric(g2,g2,g-2)
    c: Diameter(g20) = 15.5
    c: Diameter(g21) = 7.2
    c: Equal(g16,g17)
    c: Equal(g17,g18)
    c: Equal(g18,g19)
    c: DistanceY(g14,g12) = 16.5
    c: DistanceX(g15,g13) = 32
    c: Radius(g19) = 2
    c: DistanceX(g20,g21) = 62
    c: DistanceX(g13,g21) = 15
    c: Symmetric(g12,g14,g22)
    c: DistanceY(g20,g22) = 4
    c: DistanceY(g-1,g22) = 25.5
    c: DistanceX(g-1,g21) = 31
    c: DistanceX(g22,g22) = 100
    c: Coincident(g22,g21)
FEATURE [PartDesign::Pad] Pad001  label="Face.Pad.Face"
  ClaimChildren = false
  Direction = (1,1,1)
  Fit = 0
  FitJoin = 0
  InnerFit = 0
  InnerFitJoin = 0
  InnerTaperAngle = 0
  InnerTaperAngleRev = 0
  Length = 3
  Length2 = 100
  NewSolid = false
  Placement = pos=(0,0,0) rot=(1,0,0;1.5708rad)
  Profile = -> Sketch033
  Suppress = false
  TreeRank = 0
  Type = 0
  _ProfileBasedVersion = 0
  expr: Length = <<param>>.face_thickness
FEATURE [PartDesign::Chamfer] Chamfer001  label="Face.Chamfer.Screen"
  Angle = 45
  Base = -> Pad001 [Edge34]
  BaseFeature = -> Pad001
  ChamferType = 0
  FlipDirection = false
  NewSolid = false
  Placement = pos=(0,0,0) rot=(1,0,0;1.5708rad)
  Size = 2
  Size2 = 1
  SupportTransform = false
  Suppress = false
  TreeRank = 0
FEATURE [PartDesign::Chamfer] Chamfer002  label="Face.Chamfer.Screws"
  Angle = 45
  Base = -> Chamfer001 [Edge54,Edge56,Edge53,Edge55]
  BaseFeature = -> Chamfer001
  ChamferType = 0
  FlipDirection = false
  NewSolid = false
  Placement = pos=(0,0,0) rot=(1,0,0;1.5708rad)
  Size = 1.4
  Size2 = 1
  SupportTransform = false
  Suppress = false
  TreeRank = 0
FEATURE [Sketcher::SketchObject] Sketch034  label="SketchRing"
  ArcFitTolerance = 0
  AttachmentSupport = -> [XZ_Plane008]
  FullyConstrained = true
  MapMode = 5
  Placement = pos=(0,0,0) rot=(1,0,0;1.5708rad)
  Support = -> [XZ_Plane008]
  TreeRank = 0
  sketch-geometry (6):
    g0: LineSegment StartX=-1 StartY=6.25 StartZ=0 EndX=1 EndY=6.25 EndZ=0
    g1: LineSegment StartX=1 StartY=6.25 StartZ=0 EndX=1 EndY=7.75 EndZ=0
    g2: LineSegment StartX=1 StartY=7.75 StartZ=0 EndX=0.3 EndY=7.75 EndZ=0
    g3: LineSegment StartX=0.3 StartY=7.75 StartZ=0 EndX=0.3 EndY=8.75 EndZ=0
    g4: LineSegment StartX=0.3 StartY=8.75 StartZ=0 EndX=-1 EndY=8.75 EndZ=0
    g5: LineSegment StartX=-1 StartY=8.75 StartZ=0 EndX=-1 EndY=6.25 EndZ=0
  constraints (17):
    c: Coincident(g0,g1)
    c: Vertical(g1)
    c: Coincident(g1,g2)
    c: Horizontal(g2)
    c: Coincident(g2,g3)
    c: Vertical(g3)
    c: Coincident(g3,g4)
    c: Horizontal(g4)
    c: Coincident(g4,g5)
    c: Coincident(g5,g0)
    c: Vertical(g5)
    c: DistanceX(g0,g0) = 2
    c: DistanceY(g3,g3) = 1
    c: DistanceX(g4,g4) = 1.3
    c: Symmetric(g0,g0,g-2)
    c: DistanceY(g-1,g0) = 6.25
    c: DistanceY(g5,g5) = 2.5
FEATURE [PartDesign::Revolution] Revolution001  label="Ring.Revolution"
  Angle = 360
  Axis = (1,0,0)
  Base = (0,0,0)
  ClaimChildren = false
  Fit = 0
  FitJoin = 0
  InnerFit = 0
  InnerFitJoin = 0
  NewSolid = false
  Placement = pos=(0,0,0) rot=(1,0,0;1.5708rad)
  Profile = -> Sketch034
  ReferenceAxis = -> X_Axis008
  Suppress = false
  TreeRank = 0
  _ProfileBasedVersion = 0
FEATURE [PartDesign::Body] Body006  label="BodyRing"
  AutoGroupSolids = false
  ClaimAllChildren = false
  ExportMode = 0
  Group = -> [Sketch034,Revolution001]
  Origin = -> Origin008
  Tip = -> Revolution001
  TreeRank = 0
  _ExportChildren = -> [Revolution001]
  _GroupVersion = 1
FEATURE [Part::Box] Box  label="Cube"
  AttacherType = Attacher::AttachEngine3D
  Height = 18
  Length = 18
  Placement = pos=(-9,-0.25,-9) rot=(0,0,1;0rad)
  TreeRank = 0
  Width = 0.5
FEATURE [Part::FeaturePython] Slice001  # WARN: FeaturePython — macro-defined, semantics opaque (R4)
  Base = -> Body006
  Mode = 1
  Tolerance = 0
  Tools = -> [Box]
  TreeRank = 0
FEATURE [Part::FeaturePython] Slice001_child1  label="Slice001.Ring1"  # WARN: FeaturePython — macro-defined, semantics opaque (R4)
  Base = -> Slice001
  FilterType = 1
  Invert = false
  OverrideMaxVal = 0
  TreeRank = 0
  WindowFrom = 80
  WindowTo = 100
  items = 1
FEATURE [Part::FeaturePython] Slice001_child2  label="Slice001.Ring2"  # WARN: FeaturePython — macro-defined, semantics opaque (R4)
  Base = -> Slice001
  FilterType = 1
  Invert = false
  OverrideMaxVal = 0
  TreeRank = 0
  WindowFrom = 80
  WindowTo = 100
  items = 2
FEATURE [App::DocumentObjectGroup] GrExplode_Slice001  label="Ring.Exploded Slice"
  ClaimAllChildren = true
  ExportMode = 1
  Group = -> [Slice001_child1,Slice001_child2]
  TreeRank = 0
  _GroupVersion = 1
FEATURE [Sketcher::SketchObject] Sketch035
  ArcFitTolerance = 0
  AttachmentOffset = pos=(0,0,1.5) rot=(1,0,0;0rad)
  AttachmentSupport = -> [XZ_Plane007]
  ExternalGeometry = -> [Sketch033]
  FullyConstrained = true
  MapMode = 5
  Placement = pos=(0,-1.5,-3e-16) rot=(1,0,0;1.5708rad)
  Support = -> [XZ_Plane007]
  TreeRank = 0
  expr: AttachmentOffset.Base.z = <<param>>.face_thickness - 1.5
  sketch-geometry (1):
    g0: Circle CenterX=-31 CenterY=21.5 CenterZ=0 NormalX=0 NormalY=0 NormalZ=1 AngleXU=0 Radius=9
  constraints (2):
    c: Coincident(g0,g-3)
    c: Diameter(g0) = 18
FEATURE [PartDesign::Pocket] Pocket008  label="Face.Pocket.Lip"
  BaseFeature = -> Chamfer002
  ClaimChildren = false
  Fit = 0
  FitJoin = 0
  InnerFit = 0
  InnerFitJoin = 0
  InnerTaperAngle = 0
  InnerTaperAngleRev = 0
  Length = 1.5
  Length2 = 100
  NewSolid = false
  Placement = pos=(0,0,0) rot=(1,0,0;1.5708rad)
  Profile = -> Sketch035
  Reversed = true
  Suppress = false
  TreeRank = 0
  Type = 1
  _ProfileBasedVersion = 0
FEATURE [Sketcher::SketchObject] Sketch036
  ArcFitTolerance = 0
  AttachmentSupport = -> [XZ_Plane007]
  ExternalGeometry = -> [Sketch033]
  FullyConstrained = true
  MapMode = 5
  Placement = pos=(0,0,0) rot=(1,0,0;1.5708rad)
  Support = -> [XZ_Plane007]
  TreeRank = 0
  sketch-geometry (5):
    g0: ArcOfCircle CenterX=30 CenterY=19.5 CenterZ=0 NormalX=0 NormalY=0 NormalZ=1 AngleXU=0 Radius=0.75 StartAngle=1.5708 EndAngle=4.71239
    g1: ArcOfCircle CenterX=32 CenterY=19.5 CenterZ=0 NormalX=0 NormalY=0 NormalZ=1 AngleXU=0 Radius=0.75 StartAngle=4.71239 EndAngle=7.85398
    g2: LineSegment StartX=30 StartY=18.75 StartZ=0 EndX=32 EndY=18.75 EndZ=0
    g3: LineSegment StartX=30 StartY=20.25 StartZ=0 EndX=32 EndY=20.25 EndZ=0
    g4: LineSegment [constr] StartX=31 StartY=25.5 StartZ=0 EndX=31 EndY=16.5 EndZ=0
  constraints (12):
    c: Tangent(g0,g3) = 1.5708
    c: Tangent(g0,g2) = -1.5708
    c: Tangent(g2,g1) = -1.5708
    c: Tangent(g3,g1) = 1.5708
    c: Horizontal(g2)
    c: Equal(g0,g1)
    c: DistanceY(g1,g-3) = 6
    c: DistanceY(g1,g1) = 1.5
    c: DistanceX(g0,g1) = 2
    c: Coincident(g4,g-3)
    c: Symmetric(g0,g1,g4)
    c: DistanceY(g4,g4) = 9
FEATURE [PartDesign::Pocket] Pocket009  label="Face.Pocket.Notch"
  BaseFeature = -> Pocket008
  ClaimChildren = false
  Fit = 0
  FitJoin = 0
  InnerFit = 0
  InnerFitJoin = 0
  InnerTaperAngle = 0
  InnerTaperAngleRev = 0
  Length = 1
  Length2 = 100
  NewSolid = false
  Placement = pos=(0,0,0) rot=(1,0,0;1.5708rad)
  Profile = -> Sketch036
  Reversed = true
  Suppress = false
  TreeRank = 0
  Type = 0
  _ProfileBasedVersion = 0
FEATURE [PartDesign::Fillet] Fillet  label="Back.Fillet.Big"
  Base = -> Pocket [Edge63,Edge30]
  BaseFeature = -> Pocket
  NewSolid = false
  Radius = 10
  SupportTransform = false
  Suppress = false
  TreeRank = 0
  expr: Radius = <<param>>.radius_big
FEATURE [PartDesign::Fillet] Fillet004  label="Back.Fillet.Rear"
  Base = -> Fillet [Edge4]
  BaseFeature = -> Fillet
  NewSolid = false
  Radius = 2.9
  SupportTransform = false
  Suppress = false
  TreeRank = 0
FEATURE [PartDesign::Chamfer] Chamfer  label="Back.Chamfer.Screws"
  Angle = 45
  Base = -> Fillet004 [Edge9,Edge10,Edge11,Edge25,Edge26]
  BaseFeature = -> Fillet004
  ChamferType = 0
  FlipDirection = false
  NewSolid = false
  Size = 1.4
  Size2 = 1
  SupportTransform = false
  Suppress = false
  TreeRank = 0
FEATURE [PartDesign::Body] Body  label="BodyBack"
  AutoGroupSolids = false
  BaseFeature = -> Slice_child1
  ClaimAllChildren = false
  ExportMode = 0
  Group = -> [BaseFeature,Sketch032,Pocket,Fillet,Fillet004,Chamfer]
  Origin = -> Origin
  Tip = -> Chamfer
  TreeRank = 0
  _ExportChildren = -> [BaseFeature,Pocket,Fillet,Fillet004,Chamfer]
  _GroupVersion = 1
FEATURE [Sketcher::SketchObject] Sketch037
  ArcFitTolerance = 0
  AttachmentOffset = pos=(0,0,-41) rot=(0,0,1;0rad)
  AttachmentSupport = -> [XZ_Plane005]
  FullyConstrained = true
  MapMode = 5
  Placement = pos=(0,41,9.1e-15) rot=(1,0,0;1.5708rad)
  Support = -> [XZ_Plane005]
  TreeRank = 0
  expr: AttachmentOffset.Base.z = -<<param>>.mid_depth / 2
  expr: Constraints[20] = <<param>>.reart_screw_width2
  expr: Constraints[23] = <<param>>.screw_hole / 2
  expr: Constraints[24] = <<param>>.rear_screw_offset
  expr: Constraints[2] = <<param>>.bottom_height
  sketch-geometry (9):
    g0: Circle [constr] CenterX=0 CenterY=-24 CenterZ=0 NormalX=0 NormalY=0 NormalZ=1 AngleXU=0 Radius=3
    g1: LineSegment StartX=4.5 StartY=-22.8 StartZ=0 EndX=4.5 EndY=-24 EndZ=0
    g2: LineSegment StartX=4.5 StartY=-24 StartZ=0 EndX=11.5 EndY=-24 EndZ=0
    g3: LineSegment StartX=11.5 StartY=-24 StartZ=0 EndX=11.5 EndY=-22.8 EndZ=0
    g4: ArcOfCircle CenterX=5.5 CenterY=-22.8 CenterZ=0 NormalX=0 NormalY=0 NormalZ=1 AngleXU=0 Radius=1 StartAngle=1.5708 EndAngle=3.14159
    g5: ArcOfCircle CenterX=10.5 CenterY=-22.8 CenterZ=0 NormalX=0 NormalY=0 NormalZ=1 AngleXU=0 Radius=1 StartAngle=-9e-16 EndAngle=1.5708
    g6: LineSegment StartX=5.5 StartY=-21.8 StartZ=0 EndX=10.5 EndY=-21.8 EndZ=0
    g7: Circle CenterX=-27.5 CenterY=-16.6 CenterZ=0 NormalX=0 NormalY=0 NormalZ=1 AngleXU=0 Radius=1.25
    g8: Circle CenterX=27.5 CenterY=-16.6 CenterZ=0 NormalX=0 NormalY=0 NormalZ=1 AngleXU=0 Radius=1.25
  constraints (25):
    c: PointOnObject(g0,g-2)
    c: Radius(g0) = 3
    c: DistanceY(g0,g-1) = 24
    c: Vertical(g1)
    c: Coincident(g1,g2)
    c: Horizontal(g2)
    c: Coincident(g2,g3)
    c: Coincident(g5,g3)
    c: Horizontal(g6)
    c: Vertical(g3)
    c: Horizontal(g0,g1)
    c: DistanceX(g0,g1) = 4.5
    c: Equal(g3,g1)
    c: Equal(g4,g5)
    c: Radius(g5) = 1
    c: Tangent(g6,g4) = 1.5708
    c: Tangent(g6,g5) = 1.5708
    c: Tangent(g4,g1) = -1.5708
    c: DistanceY(g2,g5) = 2.2
    c: DistanceX(g1,g2) = 7
    c: DistanceX(g7,g8) = 55
    c: Symmetric(g7,g8,g-2)
    c: Equal(g7,g8)
    c: Radius(g7) = 1.25
    c: DistanceY(g0,g7) = 7.4
FEATURE [PartDesign::Pocket] Pocket010  label="Case.Pocket.Key"
  BaseFeature = -> Pocket005
  ClaimChildren = false
  Fit = 0
  FitJoin = 0
  InnerFit = 0
  InnerFitJoin = 0
  InnerTaperAngle = 0
  InnerTaperAngleRev = 0
  Length = 0
  Length2 = 100
  Midplane = true
  NewSolid = false
  Profile = -> Sketch037
  Suppress = false
  TreeRank = 0
  Type = 3
  UpToFace = -> Pocket005 [Face26]
  _ProfileBasedVersion = 0
FEATURE [PartDesign::SubtractiveLoft] SubtractiveLoft  label="Case.SubtractiveLoft"
  BaseFeature = -> Pocket010
  ClaimChildren = false
  Closed = false
  Fit = 0
  FitJoin = 0
  InnerFit = 0
  InnerFitJoin = 0
  NewSolid = false
  Profile = -> Sketch022
  Ruled = true
  Sections = -> [Sketch025,Sketch023]
  Suppress = false
  TreeRank = 0
  _ProfileBasedVersion = 0
FEATURE [PartDesign::Revolution] Revolution  label="Case.Revolution.Button"
  Angle = 360
  Axis = (-1e-16,0.309017,0.951057)
  Base = (-4.6e-15,10,30.6)
  BaseFeature = -> SubtractiveLoft
  ClaimChildren = false
  Fit = 0
  FitJoin = 0
  InnerFit = 0
  InnerFitJoin = 0
  NewSolid = false
  Profile = -> Sketch021
  ReferenceAxis = -> Sketch021 [V_Axis]
  Reversed = true
  Suppress = false
  TreeRank = 0
  _ProfileBasedVersion = 0
FEATURE [PartDesign::Pocket] Pocket007  label="Case.Pocket.Button"
  BaseFeature = -> Revolution
  ClaimChildren = false
  Fit = 0
  FitJoin = 0
  InnerFit = 0
  InnerFitJoin = 0
  InnerTaperAngle = 0
  InnerTaperAngleRev = 0
  Length = 14
  Length2 = 100
  NewSolid = false
  Profile = -> Sketch008
  Reversed = true
  Suppress = false
  TreeRank = 0
  Type = 0
  _ProfileBasedVersion = 0
FEATURE [PartDesign::Groove] Groove  label="Case.Groove.Button"
  Angle = 360
  Axis = (-1e-16,0.309017,0.951057)
  Base = (-4.1e-15,10,28.6)
  BaseFeature = -> Pocket007
  ClaimChildren = false
  Fit = 0
  FitJoin = 0
  InnerFit = 0
  InnerFitJoin = 0
  NewSolid = false
  Profile = -> Sketch027
  ReferenceAxis = -> Sketch027 [V_Axis]
  Suppress = false
  TreeRank = 0
  _ProfileBasedVersion = 0
FEATURE [PartDesign::Pocket] Pocket004  label="Case.Pocket.Screws"
  BaseFeature = -> Groove
  ClaimChildren = false
  Fit = 0
  FitJoin = 0
  InnerFit = 0
  InnerFitJoin = 0
  InnerTaperAngle = 0
  InnerTaperAngleRev = 0
  Length = 5
  Length2 = 100
  NewSolid = false
  Profile = -> Sketch026
  Suppress = false
  TreeRank = 0
  Type = 0
  _ProfileBasedVersion = 0
FEATURE [PartDesign::Pocket] Pocket003  label="Case.Pocket.Face"
  BaseFeature = -> Pocket004
  ClaimChildren = false
  Fit = 0
  FitJoin = 0
  InnerFit = 0
  InnerFitJoin = 0
  InnerTaperAngle = 0
  InnerTaperAngleRev = 0
  Length = 6
  Length2 = 100
  NewSolid = false
  Profile = -> Sketch024
  Reversed = true
  Suppress = false
  TreeRank = 0
  Type = 0
  _ProfileBasedVersion = 0
  expr: Length = <<param>>.face_thickness * 2
FEATURE [PartDesign::Fillet] Fillet005  label="Case.Fillet.Big"
  Base = -> Pocket003 [Edge122,Edge198]
  BaseFeature = -> Pocket003
  NewSolid = false
  Radius = 10
  SupportTransform = false
  Suppress = false
  TreeRank = 0
  expr: Radius = <<param>>.radius_big
FEATURE [PartDesign::Fillet] Fillet006  label="Case.Fillet.Front"
  Base = -> Fillet005 [Edge5]
  BaseFeature = -> Fillet005
  NewSolid = false
  Radius = 2
  SupportTransform = false
  Suppress = false
  TreeRank = 0
FEATURE [PartDesign::Fillet] Fillet007  label="Case.Fillet.Face"
  Base = -> Fillet006 [Edge7]
  BaseFeature = -> Fillet006
  NewSolid = false
  Radius = 2
  SupportTransform = false
  Suppress = false
  TreeRank = 0
FEATURE [PartDesign::Fillet] Fillet008  label="Case.Fillet.Button"
  Base = -> Fillet007 [Edge95]
  BaseFeature = -> Fillet007
  NewSolid = false
  Radius = 10
  SupportTransform = false
  Suppress = false
  TreeRank = 0
FEATURE [PartDesign::Body] Body004  label="BodyCase"
  AutoGroupSolids = false
  BaseFeature = -> Slice_child0
  ClaimAllChildren = false
  ExportMode = 0
  Group = -> [BaseFeature001,Sketch008,Sketch029,Sketch018,Sketch019,Sketch021,Sketch022,Sketch023,Sketch024,Sketch025,Sketch026,Sketch027,Sketch028,Sketch,Pocket001,Pad,Pocket002,Pocket006,Pocket005,Pocket010,SubtractiveLoft,Revolution,Pocket007,Groove,Pocket004,Pocket003,Fillet005,Fillet006,Fillet007,Fillet008,Sketch037]
  Origin = -> Origin005
  Tip = -> Fillet008
  TreeRank = 0
  _ExportChildren = -> [BaseFeature001,Pocket001,Pad,Pocket002,Pocket006,Pocket005,Pocket010,SubtractiveLoft,Revolution,Pocket007,Groove,Pocket004,Pocket003,Fillet005,Fillet006,Fillet007,Fillet008]
  _GroupVersion = 1
FEATURE [Mesh::Feature] Mesh  label="BodyBack (Meshed)"
  TreeRank = 0
FEATURE [Mesh::Feature] Mesh004  label="BodyCase (Meshed)"
  TreeRank = 0
FEATURE [Part::Part2DObjectPython] ShapeString  label="Face.ShapeString"  # Draft 2D object (typed FeaturePython)
  AttachmentOffset = pos=(0,7,0) rot=(0,0,1;0rad)
  AttachmentSupport = -> [XZ_Plane007]
  FontFile = <path>
  MapMode = 5
  Placement = pos=(0,-1.6e-15,7) rot=(1,0,0;1.5708rad)
  Size = 5
  String = KSGER
  Support = -> [XZ_Plane007]
  Tracking = 0
  TreeRank = 1
FEATURE [PartDesign::SubShapeBinder] Import  label="Import(ShapeString)"
  BindCopyOnChange = 0
  BindMode = 0
  ClaimChildren = false
  Context = -> Part [Body005.Import.]
  FillStyle = 0
  Fuse = false
  MakeFace = false
  OffsetFill = false
  OffsetIntersection = false
  OffsetJoinType = 0
  OffsetOpenResult = false
  PartialLoad = false
  Relative = true
  Support = -> [ShapeString]
  TreeRank = 2
  _Version = 8
FEATURE [PartDesign::Pocket] Pocket011  label="PocketName"
  BaseFeature = -> Pocket009
  ClaimChildren = false
  Fit = 0
  FitJoin = 0
  InnerFit = 0
  InnerFitJoin = 0
  InnerTaperAngle = 0
  InnerTaperAngleRev = 0
  Length = 14
  Length2 = 100
  Linearize = true
  Midplane = true
  NewSolid = false
  Placement = pos=(0,0,0) rot=(1,0,0;1.5708rad)
  Profile = -> Import
  Suppress = false
  TreeRank = 3
  Type = 0
  _ProfileBasedVersion = 1
FEATURE [PartDesign::Body] Body005  label="BodyFace"
  AutoGroupSolids = false
  ClaimAllChildren = false
  ExportMode = 0
  Group = -> [Sketch033,Pad001,Chamfer001,Chamfer002,Sketch035,Pocket008,Sketch036,Pocket009,Import,ShapeString,Pocket011]
  Origin = -> Origin007
  Placement = pos=(0,-38,0.25) rot=(1,0,0;-0.349066rad)
  Tip = -> Pocket011
  TreeRank = 0
  _ExportChildren = -> [Pad001,Chamfer001,Chamfer002,Pocket008,Pocket009,ShapeString,Pocket011]
  _GroupVersion = 1
  expr: Placement.Base.y = -<<param>>.mid_depth / 2 + <<param>>.face_thickness
  expr: Placement.Rotation.Angle = -<<param>>.front_angle
FEATURE [Mesh::Feature] Mesh005  label="BodyFaceKSGER (Meshed)"
  TreeRank = 4
FEATURE [Mesh::Feature] Mesh006  label="SliceRing (Meshed)"
  TreeRank = 5
FEATURE [Mesh::Feature] Mesh007  label="BodyFace (Meshed)"
  TreeRank = 6
FEATURE [App::DocumentObjectGroup] Group  label="Mesh"
  ClaimAllChildren = true
  ExportMode = 1
  Group = -> [Mesh,Mesh004,Mesh006,Mesh007,Mesh005]
  TreeRank = 0
  _GroupVersion = 1
FEATURE [App::Part] Part
  ClaimAllChildren = false
  ExportMode = 1
  Group = -> [Extrude,Plane002,Common,Sketch012,Loft,Slice_child1,Slice_child0,Slice,GrExplode_Slice,Sketch030,Sketch031,Group001,Spreadsheet,Body,Body004,Body005,Group,Mesh,Mesh004,Mesh005,Mesh006,Mesh007]
  Origin = -> Origin006
  TreeRank = 0
  _ExportChildren = -> [Group001,Spreadsheet,Body,Body004,Body005,Group]
  _GroupVersion = 1
note: 1 file-system path scrubbed to <path> (originals preserved in the JSON sidecar)
